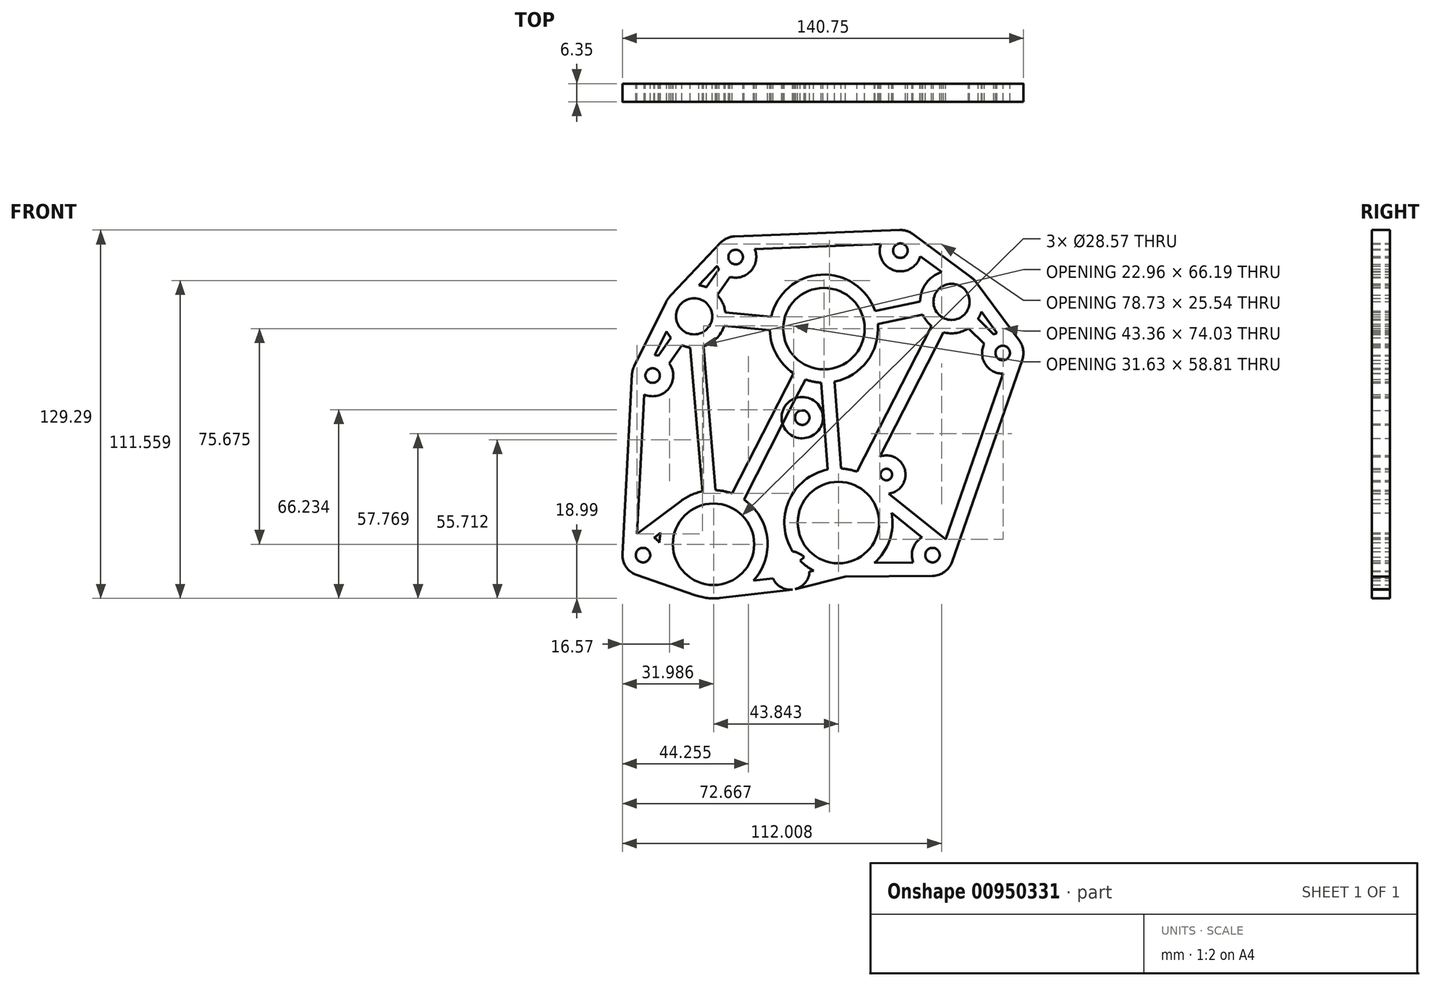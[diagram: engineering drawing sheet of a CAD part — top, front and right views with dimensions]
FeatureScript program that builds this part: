
annotation { "Feature Type Name" : "Feature", "Feature Type Description" : "" }
export const myFeature = defineFeature(function(context is Context, id is Id, definition is map)
    precondition{}
    {
        {
            var Q0;
            Q0=qCreatedBy(makeId("Front.planeOp"),FACE);
            var sketch = newSketch(context, id + "F0", { "sketchPlane" : qUnion([Q0])});
            skCircle(sketch, "E0", {"center": v(0, 0) * mm, "radius": 14.29 * mm});
            skCircle(sketch, "E1", {"center": v(-43.84, -7.62) * mm, "radius": 14.29 * mm});
            skCircle(sketch, "E2", {"center": v(-5.08, 68.06) * mm, "radius": 14.29 * mm});
            skCircle(sketch, "E3", {"center": v(39.71, 77.47) * mm, "radius": 6.35 * mm});
            skCircle(sketch, "E4", {"center": v(-50.65, 72.39) * mm, "radius": 6.35 * mm});
            skLineSegment(sketch, "E5.bottom", {"start": v(38.1, -19.05) * mm, "end": v(-76.2, -19.05) * mm, "construction": true});
            skLineSegment(sketch, "E5.top", {"start": v(38.1, 82.55) * mm, "end": v(-76.2, 82.55) * mm});
            skLineSegment(sketch, "E5.left", {"start": v(38.1, -19.05) * mm, "end": v(38.1, 82.55) * mm, "construction": true});
            skLineSegment(sketch, "E5.right", {"start": v(-76.2, -19.05) * mm, "end": v(-76.2, 82.55) * mm});
            skCircle(sketch, "E6", {"center": v(-43.84, -7.62) * mm, "radius": 18.99 * mm});
            skCircle(sketch, "E7", {"center": v(0, 0) * mm, "radius": 18.99 * mm});
            skLineSegment(sketch, "E8.bottom", {"start": v(-16.16, -9.97) * mm, "end": v(-25, -9.97) * mm});
            skLineSegment(sketch, "E8.top", {"start": v(-16.16, -5.27) * mm, "end": v(-25, -5.27) * mm});
            skLineSegment(sketch, "E8.left", {"start": v(-16.16, -9.97) * mm, "end": v(-16.16, -5.27) * mm});
            skLineSegment(sketch, "E8.right", {"start": v(-25, -9.97) * mm, "end": v(-25, -5.27) * mm});
            skCircle(sketch, "E9", {"center": v(-5.08, 68.06) * mm, "radius": 18.99 * mm});
            skCircle(sketch, "E10", {"center": v(-50.65, 72.39) * mm, "radius": 11.05 * mm});
            skLineSegment(sketch, "E11", {"start": v(-39.67, 73.7) * mm, "end": v(-40.12, 69.03) * mm, "construction": true});
            skLineSegment(sketch, "E12", {"start": v(-24.06, 67.5) * mm, "end": v(-23.61, 72.18) * mm, "construction": true});
            skLineSegment(sketch, "E13", {"start": v(-39.67, 73.7) * mm, "end": v(-23.61, 72.18) * mm});
            skLineSegment(sketch, "E14", {"start": v(-24.06, 67.5) * mm, "end": v(-40.12, 69.03) * mm});
            skLineSegment(sketch, "E15", {"start": v(-47.78, 10.95) * mm, "end": v(-43.1, 11.35) * mm, "construction": true});
            skLineSegment(sketch, "E16", {"start": v(-52.07, 61.43) * mm, "end": v(-47.39, 61.83) * mm, "construction": true});
            skLineSegment(sketch, "E17", {"start": v(-52.07, 61.43) * mm, "end": v(-47.78, 10.95) * mm});
            skLineSegment(sketch, "E18", {"start": v(-47.39, 61.83) * mm, "end": v(-43.1, 11.35) * mm});
            skCircle(sketch, "E19", {"center": v(39.71, 77.47) * mm, "radius": 11.05 * mm});
            skLineSegment(sketch, "E20.left", {"start": v(12.87, 74.23) * mm, "end": v(13.84, 69.63) * mm, "construction": true});
            skLineSegment(sketch, "E21", {"start": v(-15.76, 52.36) * mm, "end": v(-11.58, 50.22) * mm, "construction": true});
            skLineSegment(sketch, "E22", {"start": v(-37.35, 10.22) * mm, "end": v(-33.16, 8.08) * mm, "construction": true});
            skLineSegment(sketch, "E23", {"start": v(-37.35, 10.22) * mm, "end": v(-15.76, 52.36) * mm});
            skLineSegment(sketch, "E24", {"start": v(-11.58, 50.22) * mm, "end": v(-33.16, 8.08) * mm});
            skLineSegment(sketch, "E25", {"start": v(-5.08, 68.06) * mm, "end": v(0, 0) * mm, "construction": true});
            skLineSegment(sketch, "E26", {"start": v(-3.75, 18.61) * mm, "end": v(0.94, 18.96) * mm, "construction": true});
            skLineSegment(sketch, "E27", {"start": v(-6.02, 49.1) * mm, "end": v(-1.33, 49.44) * mm, "construction": true});
            skLineSegment(sketch, "E28", {"start": v(-6.02, 49.1) * mm, "end": v(-3.75, 18.61) * mm});
            skLineSegment(sketch, "E29", {"start": v(-1.33, 49.44) * mm, "end": v(0.94, 18.96) * mm});
            skLineSegment(sketch, "E30", {"start": v(6.5, 17.84) * mm, "end": v(10.69, 15.7) * mm, "construction": true});
            skLineSegment(sketch, "E31", {"start": v(32.7, 68.93) * mm, "end": v(36.88, 66.8) * mm, "construction": true});
            skLineSegment(sketch, "E32", {"start": v(32.7, 68.93) * mm, "end": v(6.5, 17.84) * mm});
            skLineSegment(sketch, "E33", {"start": v(36.88, 66.8) * mm, "end": v(10.69, 15.7) * mm});
            skCircle(sketch, "E34", {"center": v(-68.58, -11.43) * mm, "radius": 2.55 * mm});
            skCircle(sketch, "E35", {"center": v(33.02, -11.43) * mm, "radius": 2.55 * mm});
            skCircle(sketch, "E36", {"center": v(33.02, -11.43) * mm, "radius": 7.25 * mm});
            skCircle(sketch, "E37", {"center": v(-68.58, -11.43) * mm, "radius": 7.25 * mm});
            skLineSegment(sketch, "E38", {"start": v(-55.2, 7.6) * mm, "end": v(-72.92, -5.62) * mm});
            skLineSegment(sketch, "E39", {"start": v(-70.97, -18.28) * mm, "end": v(-50.09, -25.55) * mm});
            skLineSegment(sketch, "E40", {"start": v(11.88, 14.81) * mm, "end": v(37.56, -5.77) * mm});
            skCircle(sketch, "E41", {"center": v(-36.08, 93.2) * mm, "radius": 2.55 * mm});
            skCircle(sketch, "E42", {"center": v(-65.21, 51.58) * mm, "radius": 2.55 * mm});
            skLineSegment(sketch, "E43", {"start": v(-36.08, 93.2) * mm, "end": v(-65.21, 51.58) * mm, "construction": true});
            skCircle(sketch, "E44", {"center": v(57.67, 59.5) * mm, "radius": 2.55 * mm});
            skCircle(sketch, "E45", {"center": v(21.75, 95.43) * mm, "radius": 2.55 * mm});
            skCircle(sketch, "E46", {"center": v(57.67, 59.5) * mm, "radius": 7.25 * mm});
            skCircle(sketch, "E47", {"center": v(21.75, 95.43) * mm, "radius": 7.25 * mm});
            skCircle(sketch, "E48", {"center": v(-65.21, 51.58) * mm, "radius": 7.25 * mm});
            skCircle(sketch, "E49", {"center": v(-36.08, 93.2) * mm, "radius": 7.25 * mm});
            skLineSegment(sketch, "E50", {"start": v(-63.2, 58.55) * mm, "end": v(-59.35, 55.86) * mm, "construction": true});
            skLineSegment(sketch, "E51", {"start": v(-58.76, 64.9) * mm, "end": v(-54.91, 62.2) * mm, "construction": true});
            skLineSegment(sketch, "E52", {"start": v(-58.76, 64.9) * mm, "end": v(-63.2, 58.55) * mm});
            skLineSegment(sketch, "E53", {"start": v(-54.91, 62.2) * mm, "end": v(-59.35, 55.86) * mm});
            skLineSegment(sketch, "E54", {"start": v(49, 71.5) * mm, "end": v(45.68, 68.17) * mm, "construction": true});
            skLineSegment(sketch, "E55", {"start": v(51.16, 62.7) * mm, "end": v(54.48, 66.02) * mm, "construction": true});
            skLineSegment(sketch, "E56", {"start": v(51.16, 62.7) * mm, "end": v(45.68, 68.17) * mm});
            skLineSegment(sketch, "E57", {"start": v(54.48, 66.02) * mm, "end": v(49, 71.5) * mm});
            skLineSegment(sketch, "E58", {"start": v(-41.94, 88.92) * mm, "end": v(-38.09, 86.23) * mm, "construction": true});
            skLineSegment(sketch, "E59", {"start": v(-38.09, 86.23) * mm, "end": v(-42.53, 79.89) * mm});
            skLineSegment(sketch, "E60", {"start": v(-42.53, 79.89) * mm, "end": v(-46.38, 82.58) * mm, "construction": true});
            skLineSegment(sketch, "E61", {"start": v(-46.38, 82.58) * mm, "end": v(-41.94, 88.92) * mm});
            skCircle(sketch, "E62", {"center": v(0, 0) * mm, "radius": 23.81 * mm, "construction": true});
            skLineSegment(sketch, "E63", {"start": v(16.84, 16.84) * mm, "end": v(-16.84, -16.84) * mm});
            skCircle(sketch, "E64", {"center": v(-16.84, -16.84) * mm, "radius": 2.02 * mm});
            skCircle(sketch, "E65", {"center": v(16.84, 16.84) * mm, "radius": 2.02 * mm});
            skCircle(sketch, "E66", {"center": v(-16.84, -16.84) * mm, "radius": 6.72 * mm});
            skCircle(sketch, "E67", {"center": v(16.84, 16.84) * mm, "radius": 6.72 * mm});
            skLineSegment(sketch, "E68", {"start": v(21.75, 95.43) * mm, "end": v(57.67, 59.5) * mm, "construction": true});
            skLineSegment(sketch, "E69", {"start": v(12.87, 74.23) * mm, "end": v(28.66, 77.55) * mm});
            skLineSegment(sketch, "E70", {"start": v(13.84, 69.63) * mm, "end": v(29.63, 72.95) * mm});
            skLineSegment(sketch, "E71", {"start": v(29.63, 72.95) * mm, "end": v(28.66, 77.55) * mm, "construction": true});
            skLineSegment(sketch, "E72", {"start": v(18.7, 3.33) * mm, "end": v(29.32, -5.2) * mm});
            skLineSegment(sketch, "E73", {"start": v(26.26, -14.05) * mm, "end": v(12.64, -14.17) * mm});
            skLineSegment(sketch, "E74", {"start": v(-62.4, -3.64) * mm, "end": v(-64.67, -5.33) * mm});
            skLineSegment(sketch, "E75", {"start": v(-63, -16.07) * mm, "end": v(-60.35, -17) * mm});
            skCircle(sketch, "E76", {"center": v(-12.7, 36.83) * mm, "radius": 2.55 * mm});
            skCircle(sketch, "E77", {"center": v(-12.7, 36.83) * mm, "radius": 7.25 * mm});
            skLineSegment(sketch, "E78", {"start": v(-75.82, -11.04) * mm, "end": v(-72.46, 51.97) * mm});
            skLineSegment(sketch, "E79", {"start": v(-71.7, 54.8) * mm, "end": v(-60.54, 77.3) * mm});
            skLineSegment(sketch, "E80", {"start": v(-58.65, 80) * mm, "end": v(-41.33, 98.2) * mm});
            skLineSegment(sketch, "E81", {"start": v(-49, 83.32) * mm, "end": v(-42.6, 90.04) * mm});
            skLineSegment(sketch, "E82", {"start": v(-60.35, 67.11) * mm, "end": v(-64.48, 58.8) * mm});
            skLineSegment(sketch, "E83", {"start": v(-36.36, 100.44) * mm, "end": v(21.47, 102.68) * mm});
            skLineSegment(sketch, "E84", {"start": v(-29.4, 96) * mm, "end": v(14.87, 97.72) * mm});
            skLineSegment(sketch, "E85", {"start": v(26.06, 101.27) * mm, "end": v(46.27, 86.36) * mm});
            skLineSegment(sketch, "E86", {"start": v(28.73, 93.46) * mm, "end": v(36.2, 87.95) * mm});
            skLineSegment(sketch, "E87", {"start": v(48.6, 84.03) * mm, "end": v(63.5, 63.81) * mm});
            skLineSegment(sketch, "E88", {"start": v(50.19, 73.96) * mm, "end": v(55.7, 66.49) * mm});
            skLineSegment(sketch, "E89", {"start": v(39.87, -13.81) * mm, "end": v(64.52, 57.13) * mm});
            skLineSegment(sketch, "E90", {"start": v(57.86, 52.26) * mm, "end": v(37.66, -5.86) * mm});
            skLineSegment(sketch, "E91", {"start": v(-68.13, 44.94) * mm, "end": v(-70.77, -4.52) * mm});
            skLineSegment(sketch, "E92", {"start": v(33.09, -18.68) * mm, "end": v(0.18, -18.99) * mm});
            skLineSegment(sketch, "E93", {"start": v(-15.21, -23.36) * mm, "end": v(4.59, -18.42) * mm});
            skLineSegment(sketch, "E94", {"start": v(-16.06, -23.51) * mm, "end": v(-41.66, -26.48) * mm});
            skLineSegment(sketch, "E95", {"start": v(-29.78, -20.37) * mm, "end": v(-22.97, -19.58) * mm});
            skLineSegment(sketch, "E96", {"start": v(-10.13, -17.25) * mm, "end": v(-8.68, -16.89) * mm});
            skSolve(sketch);
        }
        {
            var Q0;
            {var subQ0=sQuery(id+"F0.wireOp",EDGE,"E53");Q0=makeQuery(id+"F0.imprint","IMPRINT",FACE,{"disambiguationData":[TD([[makeQuery(id+"F0.imprint","IMPRINT",EDGE,{"derivedFrom":subQ0}),-1.0]])]});}
            var Q1;
            {var subQ0=sQuery(id+"F0.wireOp",EDGE,"E59");Q1=makeQuery(id+"F0.imprint","IMPRINT",FACE,{"disambiguationData":[TD([[makeQuery(id+"F0.imprint","IMPRINT",EDGE,{"derivedFrom":subQ0}),-1.0]])]});}
            var Q2;
            {var subQ0=sQuery(id+"F0.wireOp",EDGE,"E61");Q2=makeQuery(id+"F0.imprint","IMPRINT",FACE,{"disambiguationData":[TD([[makeQuery(id+"F0.imprint","IMPRINT",EDGE,{"derivedFrom":subQ0}),-1.0]])]});}
            var Q3;
            {var subQ1=sQuery(id+"F0.wireOp",EDGE,"E9");var subQ3=sQuery(id+"F0.wireOp",EDGE,"E25");var subQ4=makeQuery(id+"F0.imprint","INTERSECT",VERTEX,{"derivedFrom":[subQ1,subQ3]});Q3=makeQuery(id+"F0.imprint","IMPRINT",FACE,{"disambiguationData":[TD([[makeQuery(id+"F0.imprint","IMPRINT",EDGE,{"disambiguationData":[TD([[subQ4,-1.0]])],"derivedFrom":subQ3}),1.0]])]});}
            var Q4;
            {var subQ1=sQuery(id+"F0.wireOp",EDGE,"E9");var subQ3=sQuery(id+"F0.wireOp",EDGE,"E25");var subQ4=makeQuery(id+"F0.imprint","INTERSECT",VERTEX,{"derivedFrom":[subQ1,subQ3]});Q4=makeQuery(id+"F0.imprint","IMPRINT",FACE,{"disambiguationData":[TD([[makeQuery(id+"F0.imprint","IMPRINT",EDGE,{"disambiguationData":[TD([[subQ4,-1.0]])],"derivedFrom":subQ3}),-1.0]])]});}
            var Q5;
            {var subQ0=sQuery(id+"F0.wireOp",EDGE,"E20.right");Q5=makeQuery(id+"F0.imprint","IMPRINT",FACE,{"disambiguationData":[TD([[makeQuery(id+"F0.imprint","IMPRINT",EDGE,{"derivedFrom":subQ0}),1.0]])]});}
            var Q6;
            {var subQ0=sQuery(id+"F0.wireOp",EDGE,"E47");var subQ1=sQuery(id+"F0.wireOp",EDGE,"E5.top");var subQ2=makeQuery(id+"F0.imprint","INTERSECT",VERTEX,{"disambiguationData":[OD(0.0)],"derivedFrom":[subQ1,subQ0]});Q6=makeQuery(id+"F0.imprint","IMPRINT",FACE,{"disambiguationData":[TD([[makeQuery(id+"F0.imprint","IMPRINT",EDGE,{"disambiguationData":[TD([[subQ2,-1.0]])],"derivedFrom":subQ1}),-1.0]])]});}
            var Q7;
            {var subQ0=sQuery(id+"F0.wireOp",EDGE,"E48");var subQ1=sQuery(id+"F0.wireOp",EDGE,"E5.right");var subQ2=makeQuery(id+"F0.imprint","INTERSECT",VERTEX,{"disambiguationData":[OD(0.0)],"derivedFrom":[subQ1,subQ0]});Q7=makeQuery(id+"F0.imprint","IMPRINT",FACE,{"disambiguationData":[TD([[makeQuery(id+"F0.imprint","IMPRINT",EDGE,{"disambiguationData":[TD([[subQ2,-1.0]])],"derivedFrom":subQ1}),1.0]])]});}
            var Q8;
            {var subQ1=sQuery(id+"F0.wireOp",EDGE,"E5.bottom");var subQ8=sQuery(id+"F0.wireOp",EDGE,"E66");var subQ11=makeQuery(id+"F0.imprint","INTERSECT",VERTEX,{"disambiguationData":[OD(1.0)],"derivedFrom":[subQ1,subQ8]});Q8=makeQuery(id+"F0.imprint","IMPRINT",FACE,{"disambiguationData":[TD([[makeQuery(id+"F0.imprint","IMPRINT",EDGE,{"disambiguationData":[TD([[subQ11,-1.0]])],"derivedFrom":subQ1}),-1.0]])]});}
            var Q9;
            {var subQ0=sQuery(id+"F0.wireOp",EDGE,"E66");var subQ1=sQuery(id+"F0.wireOp",EDGE,"E5.bottom");var subQ2=makeQuery(id+"F0.imprint","INTERSECT",VERTEX,{"disambiguationData":[OD(0.0)],"derivedFrom":[subQ1,subQ0]});Q9=makeQuery(id+"F0.imprint","IMPRINT",FACE,{"disambiguationData":[TD([[makeQuery(id+"F0.imprint","IMPRINT",EDGE,{"disambiguationData":[TD([[subQ2,1.0]])],"derivedFrom":subQ1}),1.0]])]});}
            var Q10;
            Q10=makeQuery(id+"F0.imprint","IMPRINT",FACE,{"disambiguationData":[TD([[makeQuery(id+"F0.imprint","IMPRINT",EDGE,{"derivedFrom":sQuery(id+"F0.wireOp",EDGE,"E44")}),-1.0]])]});
            var Q11;
            {var subQ0=sQuery(id+"F0.wireOp",EDGE,"E67");var subQ1=sQuery(id+"F0.wireOp",EDGE,"E46");var subQ2=makeQuery(id+"F0.imprint","INTERSECT",VERTEX,{"disambiguationData":[OD(0.0)],"derivedFrom":[subQ1,subQ0]});Q11=makeQuery(id+"F0.imprint","IMPRINT",FACE,{"disambiguationData":[TD([[makeQuery(id+"F0.imprint","IMPRINT",EDGE,{"disambiguationData":[TD([[subQ2,-1.0]])],"derivedFrom":subQ1}),1.0]])]});}
            var Q12;
            {var subQ0=sQuery(id+"F0.wireOp",EDGE,"E56");Q12=makeQuery(id+"F0.imprint","IMPRINT",FACE,{"disambiguationData":[TD([[makeQuery(id+"F0.imprint","IMPRINT",EDGE,{"derivedFrom":subQ0}),-1.0]])]});}
            var Q13;
            {var subQ3=sQuery(id+"F0.wireOp",EDGE,"VYO2AEf5-A0on-8gMK-xq1d-WM22INMwvEMz");var subQ5=sQuery(id+"F0.wireOp",EDGE,"E3");var subQ6=makeQuery(id+"F0.imprint","INTERSECT",VERTEX,{"derivedFrom":[subQ5,subQ3]});Q13=makeQuery(id+"F0.imprint","IMPRINT",FACE,{"disambiguationData":[TD([[makeQuery(id+"F0.imprint","IMPRINT",EDGE,{"disambiguationData":[TD([[subQ6,-1.0]])],"derivedFrom":subQ5}),-1.0]])]});}
            var Q14;
            {var subQ1=sQuery(id+"F0.wireOp",EDGE,"E19");var subQ3=sQuery(id+"F0.wireOp",EDGE,"VYO2AEf5-A0on-8gMK-xq1d-WM22INMwvEMz");var subQ4=makeQuery(id+"F0.imprint","INTERSECT",VERTEX,{"derivedFrom":[subQ1,subQ3]});Q14=makeQuery(id+"F0.imprint","IMPRINT",FACE,{"disambiguationData":[TD([[makeQuery(id+"F0.imprint","IMPRINT",EDGE,{"disambiguationData":[TD([[subQ4,-1.0]])],"derivedFrom":subQ3}),-1.0]])]});}
            var Q15;
            {var subQ1=sQuery(id+"F0.wireOp",EDGE,"E7");var subQ3=sQuery(id+"F0.wireOp",EDGE,"VYO2AEf5-A0on-8gMK-xq1d-WM22INMwvEMz");var subQ4=makeQuery(id+"F0.imprint","INTERSECT",VERTEX,{"derivedFrom":[subQ1,subQ3]});Q15=makeQuery(id+"F0.imprint","IMPRINT",FACE,{"disambiguationData":[TD([[makeQuery(id+"F0.imprint","IMPRINT",EDGE,{"disambiguationData":[TD([[subQ4,1.0]])],"derivedFrom":subQ3}),1.0]])]});}
            var Q16;
            {var subQ1=sQuery(id+"F0.wireOp",EDGE,"E7");var subQ3=sQuery(id+"F0.wireOp",EDGE,"VYO2AEf5-A0on-8gMK-xq1d-WM22INMwvEMz");var subQ4=makeQuery(id+"F0.imprint","INTERSECT",VERTEX,{"derivedFrom":[subQ1,subQ3]});Q16=makeQuery(id+"F0.imprint","IMPRINT",FACE,{"disambiguationData":[TD([[makeQuery(id+"F0.imprint","IMPRINT",EDGE,{"disambiguationData":[TD([[subQ4,1.0]])],"derivedFrom":subQ3}),-1.0]])]});}
            var Q17;
            {var subQ0=sQuery(id+"F0.wireOp",EDGE,"E7");var subQ1=makeQuery(id+"F0.imprint","INTERSECT",VERTEX,{"derivedFrom":[subQ0,sQuery(id+"F0.wireOp",EDGE,"E40")]});Q17=makeQuery(id+"F0.imprint","IMPRINT",FACE,{"disambiguationData":[TD([[makeQuery(id+"F0.imprint","IMPRINT",EDGE,{"disambiguationData":[TD([[subQ1,1.0]])],"derivedFrom":subQ0}),1.0]])]});}
            var Q18;
            {var subQ3=sQuery(id+"F0.wireOp",EDGE,"E63");var subQ5=sQuery(id+"F0.wireOp",EDGE,"E40");var subQ6=makeQuery(id+"F0.imprint","INTERSECT",VERTEX,{"derivedFrom":[subQ5,subQ3]});Q18=makeQuery(id+"F0.imprint","IMPRINT",FACE,{"disambiguationData":[TD([[makeQuery(id+"F0.imprint","IMPRINT",EDGE,{"disambiguationData":[TD([[subQ6,-1.0]])],"derivedFrom":subQ5}),1.0]])]});}
            var Q19;
            {var subQ5=sQuery(id+"F0.wireOp",EDGE,"E7");var subQ8=sQuery(id+"F0.wireOp",EDGE,"E40");var subQ11=makeQuery(id+"F0.imprint","INTERSECT",VERTEX,{"derivedFrom":[subQ5,subQ8]});Q19=makeQuery(id+"F0.imprint","IMPRINT",FACE,{"disambiguationData":[TD([[makeQuery(id+"F0.imprint","IMPRINT",EDGE,{"disambiguationData":[TD([[subQ11,-1.0]])],"derivedFrom":subQ5}),-1.0]])]});}
            var Q20;
            {var subQ1=sQuery(id+"F0.wireOp",EDGE,"E7");var subQ3=sQuery(id+"F0.wireOp",EDGE,"E25");var subQ4=makeQuery(id+"F0.imprint","INTERSECT",VERTEX,{"derivedFrom":[subQ1,subQ3]});Q20=makeQuery(id+"F0.imprint","IMPRINT",FACE,{"disambiguationData":[TD([[makeQuery(id+"F0.imprint","IMPRINT",EDGE,{"disambiguationData":[TD([[subQ4,1.0]])],"derivedFrom":subQ3}),-1.0]])]});}
            var Q21;
            {var subQ1=sQuery(id+"F0.wireOp",EDGE,"E7");var subQ3=sQuery(id+"F0.wireOp",EDGE,"E25");var subQ4=makeQuery(id+"F0.imprint","INTERSECT",VERTEX,{"derivedFrom":[subQ1,subQ3]});Q21=makeQuery(id+"F0.imprint","IMPRINT",FACE,{"disambiguationData":[TD([[makeQuery(id+"F0.imprint","IMPRINT",EDGE,{"disambiguationData":[TD([[subQ4,1.0]])],"derivedFrom":subQ3}),1.0]])]});}
            var Q22;
            {var subQ1=sQuery(id+"F0.wireOp",EDGE,"E19");var subQ3=sQuery(id+"F0.wireOp",EDGE,"VYO2AEf5-A0on-8gMK-xq1d-WM22INMwvEMz");var subQ4=makeQuery(id+"F0.imprint","INTERSECT",VERTEX,{"derivedFrom":[subQ1,subQ3]});Q22=makeQuery(id+"F0.imprint","IMPRINT",FACE,{"disambiguationData":[TD([[makeQuery(id+"F0.imprint","IMPRINT",EDGE,{"disambiguationData":[TD([[subQ4,-1.0]])],"derivedFrom":subQ3}),1.0]])]});}
            var Q23;
            {var subQ0=sQuery(id+"F0.wireOp",EDGE,"E63");var subQ1=sQuery(id+"F0.wireOp",EDGE,"E7");var subQ2=makeQuery(id+"F0.imprint","INTERSECT",VERTEX,{"disambiguationData":[OD(0.0)],"derivedFrom":[subQ1,subQ0]});Q23=makeQuery(id+"F0.imprint","IMPRINT",FACE,{"disambiguationData":[TD([[makeQuery(id+"F0.imprint","IMPRINT",EDGE,{"disambiguationData":[TD([[subQ2,1.0]])],"derivedFrom":subQ1}),-1.0]])]});}
            var Q24;
            {var subQ3=sQuery(id+"F0.wireOp",EDGE,"VYO2AEf5-A0on-8gMK-xq1d-WM22INMwvEMz");var subQ5=sQuery(id+"F0.wireOp",EDGE,"E0");var subQ6=makeQuery(id+"F0.imprint","INTERSECT",VERTEX,{"derivedFrom":[subQ5,subQ3]});Q24=makeQuery(id+"F0.imprint","IMPRINT",FACE,{"disambiguationData":[TD([[makeQuery(id+"F0.imprint","IMPRINT",EDGE,{"disambiguationData":[TD([[subQ6,1.0]])],"derivedFrom":subQ5}),-1.0]])]});}
            var Q25;
            {var subQ5=sQuery(id+"F0.wireOp",EDGE,"E0");var subQ9=sQuery(id+"F0.wireOp",EDGE,"VYO2AEf5-A0on-8gMK-xq1d-WM22INMwvEMz");var subQ10=makeQuery(id+"F0.imprint","INTERSECT",VERTEX,{"derivedFrom":[subQ5,subQ9]});Q25=makeQuery(id+"F0.imprint","IMPRINT",FACE,{"disambiguationData":[TD([[makeQuery(id+"F0.imprint","IMPRINT",EDGE,{"disambiguationData":[TD([[subQ10,-1.0]])],"derivedFrom":subQ5}),-1.0]])]});}
            var Q26;
            {var subQ1=sQuery(id+"F0.wireOp",EDGE,"E7");var subQ3=sQuery(id+"F0.wireOp",EDGE,"VYO2AEf5-A0on-8gMK-xq1d-WM22INMwvEMz");var subQ4=makeQuery(id+"F0.imprint","INTERSECT",VERTEX,{"derivedFrom":[subQ1,subQ3]});Q26=makeQuery(id+"F0.imprint","IMPRINT",FACE,{"disambiguationData":[TD([[makeQuery(id+"F0.imprint","IMPRINT",EDGE,{"disambiguationData":[TD([[subQ4,-1.0]])],"derivedFrom":subQ3}),-1.0]])]});}
            var Q27;
            {var subQ1=sQuery(id+"F0.wireOp",EDGE,"E7");var subQ3=sQuery(id+"F0.wireOp",EDGE,"VYO2AEf5-A0on-8gMK-xq1d-WM22INMwvEMz");var subQ4=makeQuery(id+"F0.imprint","INTERSECT",VERTEX,{"derivedFrom":[subQ1,subQ3]});Q27=makeQuery(id+"F0.imprint","IMPRINT",FACE,{"disambiguationData":[TD([[makeQuery(id+"F0.imprint","IMPRINT",EDGE,{"disambiguationData":[TD([[subQ4,-1.0]])],"derivedFrom":subQ3}),1.0]])]});}
            var Q28;
            {var subQ1=sQuery(id+"F0.wireOp",EDGE,"E7");var subQ3=sQuery(id+"F0.wireOp",EDGE,"E25");var subQ4=makeQuery(id+"F0.imprint","INTERSECT",VERTEX,{"derivedFrom":[subQ1,subQ3]});Q28=makeQuery(id+"F0.imprint","IMPRINT",FACE,{"disambiguationData":[TD([[makeQuery(id+"F0.imprint","IMPRINT",EDGE,{"disambiguationData":[TD([[subQ4,-1.0]])],"derivedFrom":subQ3}),1.0]])]});}
            var Q29;
            {var subQ1=sQuery(id+"F0.wireOp",EDGE,"E7");var subQ3=sQuery(id+"F0.wireOp",EDGE,"E25");var subQ4=makeQuery(id+"F0.imprint","INTERSECT",VERTEX,{"derivedFrom":[subQ1,subQ3]});Q29=makeQuery(id+"F0.imprint","IMPRINT",FACE,{"disambiguationData":[TD([[makeQuery(id+"F0.imprint","IMPRINT",EDGE,{"disambiguationData":[TD([[subQ4,-1.0]])],"derivedFrom":subQ3}),-1.0]])]});}
            var Q30;
            {var subQ0=sQuery(id+"F0.wireOp",EDGE,"E55");var subQ1=sQuery(id+"F0.wireOp",EDGE,"QEKIW3ol-zFeQ-8mqy-IqnZ-AELnMHeZj292");var subQ2=makeQuery(id+"F0.imprint","INTERSECT",VERTEX,{"derivedFrom":[subQ1,subQ0]});Q30=makeQuery(id+"F0.imprint","IMPRINT",FACE,{"disambiguationData":[TD([[makeQuery(id+"F0.imprint","IMPRINT",EDGE,{"disambiguationData":[TD([[subQ2,1.0]])],"derivedFrom":subQ1}),-1.0]])]});}
            var Q31;
            {var subQ0=sQuery(id+"F0.wireOp",EDGE,"E55");var subQ1=sQuery(id+"F0.wireOp",EDGE,"QEKIW3ol-zFeQ-8mqy-IqnZ-AELnMHeZj292");var subQ2=makeQuery(id+"F0.imprint","INTERSECT",VERTEX,{"derivedFrom":[subQ1,subQ0]});Q31=makeQuery(id+"F0.imprint","IMPRINT",FACE,{"disambiguationData":[TD([[makeQuery(id+"F0.imprint","IMPRINT",EDGE,{"disambiguationData":[TD([[subQ2,1.0]])],"derivedFrom":subQ1}),1.0]])]});}
            var Q32;
            {var subQ1=sQuery(id+"F0.wireOp",EDGE,"E19");var subQ3=sQuery(id+"F0.wireOp",EDGE,"VYO2AEf5-A0on-8gMK-xq1d-WM22INMwvEMz");var subQ4=makeQuery(id+"F0.imprint","INTERSECT",VERTEX,{"derivedFrom":[subQ1,subQ3]});Q32=makeQuery(id+"F0.imprint","IMPRINT",FACE,{"disambiguationData":[TD([[makeQuery(id+"F0.imprint","IMPRINT",EDGE,{"disambiguationData":[TD([[subQ4,1.0]])],"derivedFrom":subQ3}),-1.0]])]});}
            var Q33;
            {var subQ1=sQuery(id+"F0.wireOp",EDGE,"E19");var subQ3=sQuery(id+"F0.wireOp",EDGE,"VYO2AEf5-A0on-8gMK-xq1d-WM22INMwvEMz");var subQ4=makeQuery(id+"F0.imprint","INTERSECT",VERTEX,{"derivedFrom":[subQ1,subQ3]});Q33=makeQuery(id+"F0.imprint","IMPRINT",FACE,{"disambiguationData":[TD([[makeQuery(id+"F0.imprint","IMPRINT",EDGE,{"disambiguationData":[TD([[subQ4,1.0]])],"derivedFrom":subQ3}),1.0]])]});}
            var Q34;
            {var subQ1=sQuery(id+"F0.wireOp",EDGE,"E19");var subQ3=sQuery(id+"F0.wireOp",EDGE,"QEKIW3ol-zFeQ-8mqy-IqnZ-AELnMHeZj292");var subQ4=makeQuery(id+"F0.imprint","INTERSECT",VERTEX,{"disambiguationData":[OD(1.0)],"derivedFrom":[subQ1,subQ3]});Q34=makeQuery(id+"F0.imprint","IMPRINT",FACE,{"disambiguationData":[TD([[makeQuery(id+"F0.imprint","IMPRINT",EDGE,{"disambiguationData":[TD([[subQ4,1.0]])],"derivedFrom":subQ3}),-1.0]])]});}
            var Q35;
            {var subQ1=sQuery(id+"F0.wireOp",EDGE,"E19");var subQ3=sQuery(id+"F0.wireOp",EDGE,"QEKIW3ol-zFeQ-8mqy-IqnZ-AELnMHeZj292");var subQ4=makeQuery(id+"F0.imprint","INTERSECT",VERTEX,{"disambiguationData":[OD(1.0)],"derivedFrom":[subQ1,subQ3]});Q35=makeQuery(id+"F0.imprint","IMPRINT",FACE,{"disambiguationData":[TD([[makeQuery(id+"F0.imprint","IMPRINT",EDGE,{"disambiguationData":[TD([[subQ4,1.0]])],"derivedFrom":subQ3}),1.0]])]});}
            var Q36;
            {var subQ0=sQuery(id+"F0.wireOp",EDGE,"E20.left");Q36=makeQuery(id+"F0.imprint","IMPRINT",FACE,{"disambiguationData":[TD([[makeQuery(id+"F0.imprint","IMPRINT",EDGE,{"derivedFrom":subQ0}),1.0]])]});}
            var Q37;
            {var subQ0=sQuery(id+"F0.wireOp",EDGE,"E20.right");Q37=makeQuery(id+"F0.imprint","IMPRINT",FACE,{"disambiguationData":[TD([[makeQuery(id+"F0.imprint","IMPRINT",EDGE,{"derivedFrom":subQ0}),-1.0]])]});}
            var Q38;
            {var subQ1=sQuery(id+"F0.wireOp",EDGE,"E19");var subQ3=sQuery(id+"F0.wireOp",EDGE,"QEKIW3ol-zFeQ-8mqy-IqnZ-AELnMHeZj292");var subQ4=makeQuery(id+"F0.imprint","INTERSECT",VERTEX,{"disambiguationData":[OD(0.0)],"derivedFrom":[subQ1,subQ3]});Q38=makeQuery(id+"F0.imprint","IMPRINT",FACE,{"disambiguationData":[TD([[makeQuery(id+"F0.imprint","IMPRINT",EDGE,{"disambiguationData":[TD([[subQ4,-1.0]])],"derivedFrom":subQ3}),-1.0]])]});}
            var Q39;
            {var subQ1=sQuery(id+"F0.wireOp",EDGE,"E19");var subQ3=sQuery(id+"F0.wireOp",EDGE,"QEKIW3ol-zFeQ-8mqy-IqnZ-AELnMHeZj292");var subQ4=makeQuery(id+"F0.imprint","INTERSECT",VERTEX,{"disambiguationData":[OD(0.0)],"derivedFrom":[subQ1,subQ3]});Q39=makeQuery(id+"F0.imprint","IMPRINT",FACE,{"disambiguationData":[TD([[makeQuery(id+"F0.imprint","IMPRINT",EDGE,{"disambiguationData":[TD([[subQ4,-1.0]])],"derivedFrom":subQ3}),1.0]])]});}
            var Q40;
            {var subQ0=sQuery(id+"F0.wireOp",EDGE,"PWp1EvH2-qaDC-40DG-vf9U-hu9o8N1M8XT3");var subQ1=sQuery(id+"F0.wireOp",EDGE,"QEKIW3ol-zFeQ-8mqy-IqnZ-AELnMHeZj292");var subQ2=makeQuery(id+"F0.imprint","INTERSECT",VERTEX,{"derivedFrom":[subQ1,subQ0]});Q40=makeQuery(id+"F0.imprint","IMPRINT",FACE,{"disambiguationData":[TD([[makeQuery(id+"F0.imprint","IMPRINT",EDGE,{"disambiguationData":[TD([[subQ2,-1.0]])],"derivedFrom":subQ1}),1.0]])]});}
            var Q41;
            {var subQ0=sQuery(id+"F0.wireOp",EDGE,"PWp1EvH2-qaDC-40DG-vf9U-hu9o8N1M8XT3");var subQ1=sQuery(id+"F0.wireOp",EDGE,"QEKIW3ol-zFeQ-8mqy-IqnZ-AELnMHeZj292");var subQ2=makeQuery(id+"F0.imprint","INTERSECT",VERTEX,{"derivedFrom":[subQ1,subQ0]});Q41=makeQuery(id+"F0.imprint","IMPRINT",FACE,{"disambiguationData":[TD([[makeQuery(id+"F0.imprint","IMPRINT",EDGE,{"disambiguationData":[TD([[subQ2,-1.0]])],"derivedFrom":subQ1}),-1.0]])]});}
            var Q42;
            {var subQ3=sQuery(id+"F0.wireOp",EDGE,"E13");Q42=makeQuery(id+"F0.imprint","IMPRINT",FACE,{"disambiguationData":[TD([[makeQuery(id+"F0.imprint","IMPRINT",EDGE,{"derivedFrom":subQ3}),-1.0]])]});}
            var Q43;
            {var subQ0=sQuery(id+"F0.wireOp",EDGE,"E50");var subQ1=sQuery(id+"F0.wireOp",EDGE,"E43");var subQ2=makeQuery(id+"F0.imprint","INTERSECT",VERTEX,{"derivedFrom":[subQ1,subQ0]});Q43=makeQuery(id+"F0.imprint","IMPRINT",FACE,{"disambiguationData":[TD([[makeQuery(id+"F0.imprint","IMPRINT",EDGE,{"disambiguationData":[TD([[subQ2,1.0]])],"derivedFrom":subQ1}),-1.0]])]});}
            var Q44;
            {var subQ0=sQuery(id+"F0.wireOp",EDGE,"E50");var subQ1=sQuery(id+"F0.wireOp",EDGE,"E43");var subQ2=makeQuery(id+"F0.imprint","INTERSECT",VERTEX,{"derivedFrom":[subQ1,subQ0]});Q44=makeQuery(id+"F0.imprint","IMPRINT",FACE,{"disambiguationData":[TD([[makeQuery(id+"F0.imprint","IMPRINT",EDGE,{"disambiguationData":[TD([[subQ2,1.0]])],"derivedFrom":subQ1}),1.0]])]});}
            var Q45;
            {var subQ1=sQuery(id+"F0.wireOp",EDGE,"E10");var subQ3=sQuery(id+"F0.wireOp",EDGE,"E43");var subQ4=makeQuery(id+"F0.imprint","INTERSECT",VERTEX,{"disambiguationData":[OD(1.0)],"derivedFrom":[subQ1,subQ3]});Q45=makeQuery(id+"F0.imprint","IMPRINT",FACE,{"disambiguationData":[TD([[makeQuery(id+"F0.imprint","IMPRINT",EDGE,{"disambiguationData":[TD([[subQ4,1.0]])],"derivedFrom":subQ3}),-1.0]])]});}
            var Q46;
            {var subQ1=sQuery(id+"F0.wireOp",EDGE,"E10");var subQ3=sQuery(id+"F0.wireOp",EDGE,"E43");var subQ4=makeQuery(id+"F0.imprint","INTERSECT",VERTEX,{"disambiguationData":[OD(1.0)],"derivedFrom":[subQ1,subQ3]});Q46=makeQuery(id+"F0.imprint","IMPRINT",FACE,{"disambiguationData":[TD([[makeQuery(id+"F0.imprint","IMPRINT",EDGE,{"disambiguationData":[TD([[subQ4,1.0]])],"derivedFrom":subQ3}),1.0]])]});}
            var Q47;
            {var subQ1=sQuery(id+"F0.wireOp",EDGE,"E10");var subQ3=sQuery(id+"F0.wireOp",EDGE,"DAOfpOoV-ewgr-EIjx-MOBx-atSazLD0E7Ij");var subQ4=makeQuery(id+"F0.imprint","INTERSECT",VERTEX,{"derivedFrom":[subQ1,subQ3]});Q47=makeQuery(id+"F0.imprint","IMPRINT",FACE,{"disambiguationData":[TD([[makeQuery(id+"F0.imprint","IMPRINT",EDGE,{"disambiguationData":[TD([[subQ4,1.0]])],"derivedFrom":subQ3}),-1.0]])]});}
            var Q48;
            {var subQ1=sQuery(id+"F0.wireOp",EDGE,"E10");var subQ3=sQuery(id+"F0.wireOp",EDGE,"DAOfpOoV-ewgr-EIjx-MOBx-atSazLD0E7Ij");var subQ4=makeQuery(id+"F0.imprint","INTERSECT",VERTEX,{"derivedFrom":[subQ1,subQ3]});Q48=makeQuery(id+"F0.imprint","IMPRINT",FACE,{"disambiguationData":[TD([[makeQuery(id+"F0.imprint","IMPRINT",EDGE,{"disambiguationData":[TD([[subQ4,1.0]])],"derivedFrom":subQ3}),1.0]])]});}
            var Q49;
            {var subQ0=sQuery(id+"F0.wireOp",EDGE,"E11");Q49=makeQuery(id+"F0.imprint","IMPRINT",FACE,{"disambiguationData":[TD([[makeQuery(id+"F0.imprint","IMPRINT",EDGE,{"derivedFrom":subQ0}),1.0]])]});}
            var Q50;
            {var subQ0=sQuery(id+"F0.wireOp",EDGE,"E12");Q50=makeQuery(id+"F0.imprint","IMPRINT",FACE,{"disambiguationData":[TD([[makeQuery(id+"F0.imprint","IMPRINT",EDGE,{"derivedFrom":subQ0}),1.0]])]});}
            var Q51;
            {var subQ0=sQuery(id+"F0.wireOp",EDGE,"E63");var subQ1=sQuery(id+"F0.wireOp",EDGE,"E7");var subQ2=makeQuery(id+"F0.imprint","INTERSECT",VERTEX,{"disambiguationData":[OD(1.0)],"derivedFrom":[subQ1,subQ0]});Q51=makeQuery(id+"F0.imprint","IMPRINT",FACE,{"disambiguationData":[TD([[makeQuery(id+"F0.imprint","IMPRINT",EDGE,{"disambiguationData":[TD([[subQ2,-1.0]])],"derivedFrom":subQ1}),1.0]])]});}
            var Q52;
            {var subQ0=sQuery(id+"F0.wireOp",EDGE,"E66");var subQ1=sQuery(id+"F0.wireOp",EDGE,"E5.bottom");var subQ2=makeQuery(id+"F0.imprint","INTERSECT",VERTEX,{"disambiguationData":[OD(1.0)],"derivedFrom":[subQ1,subQ0]});Q52=makeQuery(id+"F0.imprint","IMPRINT",FACE,{"disambiguationData":[TD([[makeQuery(id+"F0.imprint","IMPRINT",EDGE,{"disambiguationData":[TD([[subQ2,-1.0]])],"derivedFrom":subQ1}),1.0]])]});}
            var Q53;
            {var subQ1=sQuery(id+"F0.wireOp",EDGE,"E6");var subQ3=sQuery(id+"F0.wireOp",EDGE,"DAOfpOoV-ewgr-EIjx-MOBx-atSazLD0E7Ij");var subQ4=makeQuery(id+"F0.imprint","INTERSECT",VERTEX,{"derivedFrom":[subQ1,subQ3]});Q53=makeQuery(id+"F0.imprint","IMPRINT",FACE,{"disambiguationData":[TD([[makeQuery(id+"F0.imprint","IMPRINT",EDGE,{"disambiguationData":[TD([[subQ4,-1.0]])],"derivedFrom":subQ3}),-1.0]])]});}
            var Q54;
            {var subQ1=sQuery(id+"F0.wireOp",EDGE,"E6");var subQ3=sQuery(id+"F0.wireOp",EDGE,"DAOfpOoV-ewgr-EIjx-MOBx-atSazLD0E7Ij");var subQ4=makeQuery(id+"F0.imprint","INTERSECT",VERTEX,{"derivedFrom":[subQ1,subQ3]});Q54=makeQuery(id+"F0.imprint","IMPRINT",FACE,{"disambiguationData":[TD([[makeQuery(id+"F0.imprint","IMPRINT",EDGE,{"disambiguationData":[TD([[subQ4,-1.0]])],"derivedFrom":subQ3}),1.0]])]});}
            var Q55;
            {var subQ1=sQuery(id+"F0.wireOp",EDGE,"E6");var subQ3=sQuery(id+"F0.wireOp",EDGE,"iRxx2WUk-GL6D-XYzB-BCGU-y0DAeOXOSD90");var subQ4=makeQuery(id+"F0.imprint","INTERSECT",VERTEX,{"derivedFrom":[subQ1,subQ3]});Q55=makeQuery(id+"F0.imprint","IMPRINT",FACE,{"disambiguationData":[TD([[makeQuery(id+"F0.imprint","IMPRINT",EDGE,{"disambiguationData":[TD([[subQ4,1.0]])],"derivedFrom":subQ3}),1.0]])]});}
            var Q56;
            {var subQ1=sQuery(id+"F0.wireOp",EDGE,"E6");var subQ3=sQuery(id+"F0.wireOp",EDGE,"iRxx2WUk-GL6D-XYzB-BCGU-y0DAeOXOSD90");var subQ4=makeQuery(id+"F0.imprint","INTERSECT",VERTEX,{"derivedFrom":[subQ1,subQ3]});Q56=makeQuery(id+"F0.imprint","IMPRINT",FACE,{"disambiguationData":[TD([[makeQuery(id+"F0.imprint","IMPRINT",EDGE,{"disambiguationData":[TD([[subQ4,1.0]])],"derivedFrom":subQ3}),-1.0]])]});}
            var Q57;
            {var subQ1=sQuery(id+"F0.wireOp",EDGE,"E9");var subQ3=sQuery(id+"F0.wireOp",EDGE,"iRxx2WUk-GL6D-XYzB-BCGU-y0DAeOXOSD90");var subQ4=makeQuery(id+"F0.imprint","INTERSECT",VERTEX,{"derivedFrom":[subQ1,subQ3]});Q57=makeQuery(id+"F0.imprint","IMPRINT",FACE,{"disambiguationData":[TD([[makeQuery(id+"F0.imprint","IMPRINT",EDGE,{"disambiguationData":[TD([[subQ4,-1.0]])],"derivedFrom":subQ3}),1.0]])]});}
            var Q58;
            {var subQ1=sQuery(id+"F0.wireOp",EDGE,"E9");var subQ3=sQuery(id+"F0.wireOp",EDGE,"iRxx2WUk-GL6D-XYzB-BCGU-y0DAeOXOSD90");var subQ4=makeQuery(id+"F0.imprint","INTERSECT",VERTEX,{"derivedFrom":[subQ1,subQ3]});Q58=makeQuery(id+"F0.imprint","IMPRINT",FACE,{"disambiguationData":[TD([[makeQuery(id+"F0.imprint","IMPRINT",EDGE,{"disambiguationData":[TD([[subQ4,-1.0]])],"derivedFrom":subQ3}),-1.0]])]});}
            var Q59;
            {var subQ1=sQuery(id+"F0.wireOp",EDGE,"E9");var subQ3=sQuery(id+"F0.wireOp",EDGE,"E25");var subQ4=makeQuery(id+"F0.imprint","INTERSECT",VERTEX,{"derivedFrom":[subQ1,subQ3]});Q59=makeQuery(id+"F0.imprint","IMPRINT",FACE,{"disambiguationData":[TD([[makeQuery(id+"F0.imprint","IMPRINT",EDGE,{"disambiguationData":[TD([[subQ4,1.0]])],"derivedFrom":subQ3}),-1.0]])]});}
            var Q60;
            {var subQ1=sQuery(id+"F0.wireOp",EDGE,"E9");var subQ3=sQuery(id+"F0.wireOp",EDGE,"E25");var subQ4=makeQuery(id+"F0.imprint","INTERSECT",VERTEX,{"derivedFrom":[subQ1,subQ3]});Q60=makeQuery(id+"F0.imprint","IMPRINT",FACE,{"disambiguationData":[TD([[makeQuery(id+"F0.imprint","IMPRINT",EDGE,{"disambiguationData":[TD([[subQ4,1.0]])],"derivedFrom":subQ3}),1.0]])]});}
            var Q61;
            {var subQ1=sQuery(id+"F0.wireOp",EDGE,"E10");var subQ3=sQuery(id+"F0.wireOp",EDGE,"E43");var subQ4=makeQuery(id+"F0.imprint","INTERSECT",VERTEX,{"disambiguationData":[OD(0.0)],"derivedFrom":[subQ1,subQ3]});Q61=makeQuery(id+"F0.imprint","IMPRINT",FACE,{"disambiguationData":[TD([[makeQuery(id+"F0.imprint","IMPRINT",EDGE,{"disambiguationData":[TD([[subQ4,-1.0]])],"derivedFrom":subQ3}),-1.0]])]});}
            var Q62;
            {var subQ1=sQuery(id+"F0.wireOp",EDGE,"E10");var subQ3=sQuery(id+"F0.wireOp",EDGE,"E43");var subQ4=makeQuery(id+"F0.imprint","INTERSECT",VERTEX,{"disambiguationData":[OD(0.0)],"derivedFrom":[subQ1,subQ3]});Q62=makeQuery(id+"F0.imprint","IMPRINT",FACE,{"disambiguationData":[TD([[makeQuery(id+"F0.imprint","IMPRINT",EDGE,{"disambiguationData":[TD([[subQ4,-1.0]])],"derivedFrom":subQ3}),1.0]])]});}
            var Q63;
            {var subQ0=sQuery(id+"F0.wireOp",EDGE,"E58");var subQ1=sQuery(id+"F0.wireOp",EDGE,"E43");var subQ2=makeQuery(id+"F0.imprint","INTERSECT",VERTEX,{"derivedFrom":[subQ1,subQ0]});Q63=makeQuery(id+"F0.imprint","IMPRINT",FACE,{"disambiguationData":[TD([[makeQuery(id+"F0.imprint","IMPRINT",EDGE,{"disambiguationData":[TD([[subQ2,-1.0]])],"derivedFrom":subQ1}),-1.0]])]});}
            var Q64;
            {var subQ0=sQuery(id+"F0.wireOp",EDGE,"E58");var subQ1=sQuery(id+"F0.wireOp",EDGE,"E43");var subQ2=makeQuery(id+"F0.imprint","INTERSECT",VERTEX,{"derivedFrom":[subQ1,subQ0]});Q64=makeQuery(id+"F0.imprint","IMPRINT",FACE,{"disambiguationData":[TD([[makeQuery(id+"F0.imprint","IMPRINT",EDGE,{"disambiguationData":[TD([[subQ2,-1.0]])],"derivedFrom":subQ1}),1.0]])]});}
            var Q65;
            {var subQ0=sQuery(id+"F0.wireOp",EDGE,"E8.right");Q65=makeQuery(id+"F0.imprint","IMPRINT",FACE,{"disambiguationData":[TD([[makeQuery(id+"F0.imprint","IMPRINT",EDGE,{"derivedFrom":subQ0}),-1.0]])]});}
            var Q66;
            {var subQ0=sQuery(id+"F0.wireOp",EDGE,"E8.left");Q66=makeQuery(id+"F0.imprint","IMPRINT",FACE,{"disambiguationData":[TD([[makeQuery(id+"F0.imprint","IMPRINT",EDGE,{"derivedFrom":subQ0}),1.0]])]});}
            var Q67;
            {var subQ0=sQuery(id+"F0.wireOp",EDGE,"E8.right");Q67=makeQuery(id+"F0.imprint","IMPRINT",FACE,{"disambiguationData":[TD([[makeQuery(id+"F0.imprint","IMPRINT",EDGE,{"derivedFrom":subQ0}),1.0]])]});}
            var Q68;
            {var subQ0=sQuery(id+"F0.wireOp",EDGE,"E54");Q68=makeQuery(id+"F0.imprint","IMPRINT",FACE,{"disambiguationData":[TD([[makeQuery(id+"F0.imprint","IMPRINT",EDGE,{"derivedFrom":subQ0}),1.0]])]});}
            var Q69;
            {var subQ0=sQuery(id+"F0.wireOp",EDGE,"E55");Q69=makeQuery(id+"F0.imprint","IMPRINT",FACE,{"disambiguationData":[TD([[makeQuery(id+"F0.imprint","IMPRINT",EDGE,{"derivedFrom":subQ0}),1.0]])]});}
            var Q70;
            {var subQ0=sQuery(id+"F0.wireOp",EDGE,"PWp1EvH2-qaDC-40DG-vf9U-hu9o8N1M8XT3");Q70=makeQuery(id+"F0.imprint","IMPRINT",FACE,{"disambiguationData":[TD([[makeQuery(id+"F0.imprint","IMPRINT",EDGE,{"derivedFrom":subQ0}),1.0]])]});}
            var Q71;
            {var subQ0=sQuery(id+"F0.wireOp",EDGE,"reiyEHRU-APE3-DGhp-Yd7A-jMOsKlnvIUoY");Q71=makeQuery(id+"F0.imprint","IMPRINT",FACE,{"disambiguationData":[TD([[makeQuery(id+"F0.imprint","IMPRINT",EDGE,{"derivedFrom":subQ0}),1.0]])]});}
            var Q72;
            {var subQ3=sQuery(id+"F0.wireOp",EDGE,"E30");Q72=makeQuery(id+"F0.imprint","IMPRINT",FACE,{"disambiguationData":[TD([[makeQuery(id+"F0.imprint","IMPRINT",EDGE,{"derivedFrom":subQ3}),-1.0]])]});}
            var Q73;
            {var subQ0=sQuery(id+"F0.wireOp",EDGE,"E31");Q73=makeQuery(id+"F0.imprint","IMPRINT",FACE,{"disambiguationData":[TD([[makeQuery(id+"F0.imprint","IMPRINT",EDGE,{"derivedFrom":subQ0}),1.0]])]});}
            var Q74;
            {var subQ0=sQuery(id+"F0.wireOp",EDGE,"E32");var subQ6=sQuery(id+"F0.wireOp",EDGE,"E62");var subQ7=makeQuery(id+"F0.imprint","INTERSECT",VERTEX,{"derivedFrom":[subQ0,subQ6]});Q74=makeQuery(id+"F0.imprint","IMPRINT",FACE,{"disambiguationData":[TD([[makeQuery(id+"F0.imprint","IMPRINT",EDGE,{"disambiguationData":[TD([[subQ7,1.0]])],"derivedFrom":subQ6}),-1.0]])]});}
            var Q75;
            {var subQ0=sQuery(id+"F0.wireOp",EDGE,"E77");var subQ1=sQuery(id+"F0.wireOp",EDGE,"E25");var subQ2=makeQuery(id+"F0.imprint","INTERSECT",VERTEX,{"disambiguationData":[OD(1.0)],"derivedFrom":[subQ1,subQ0]});Q75=makeQuery(id+"F0.imprint","IMPRINT",FACE,{"disambiguationData":[TD([[makeQuery(id+"F0.imprint","IMPRINT",EDGE,{"disambiguationData":[TD([[subQ2,-1.0]])],"derivedFrom":subQ1}),-1.0]])]});}
            var Q76;
            {var subQ1=sQuery(id+"F0.wireOp",EDGE,"E46");var subQ5=sQuery(id+"F0.wireOp",EDGE,"E5.left");var subQ6=makeQuery(id+"F0.imprint","INTERSECT",VERTEX,{"disambiguationData":[OD(1.0)],"derivedFrom":[subQ5,subQ1]});Q76=makeQuery(id+"F0.imprint","IMPRINT",FACE,{"disambiguationData":[TD([[makeQuery(id+"F0.imprint","IMPRINT",EDGE,{"disambiguationData":[TD([[subQ6,1.0]])],"derivedFrom":subQ5}),1.0]])]});}
            var Q77;
            {var subQ1=sQuery(id+"F0.wireOp",EDGE,"E47");var subQ7=sQuery(id+"F0.wireOp",EDGE,"E5.top");var subQ9=makeQuery(id+"F0.imprint","INTERSECT",VERTEX,{"disambiguationData":[OD(1.0)],"derivedFrom":[subQ7,subQ1]});Q77=makeQuery(id+"F0.imprint","IMPRINT",FACE,{"disambiguationData":[TD([[makeQuery(id+"F0.imprint","IMPRINT",EDGE,{"disambiguationData":[TD([[subQ9,1.0]])],"derivedFrom":subQ7}),1.0]])]});}
            var Q78;
            {var subQ1=sQuery(id+"F0.wireOp",EDGE,"E49");var subQ3=sQuery(id+"F0.wireOp",EDGE,"E5.top");var subQ4=makeQuery(id+"F0.imprint","INTERSECT",VERTEX,{"disambiguationData":[OD(1.0)],"derivedFrom":[subQ3,subQ1]});Q78=makeQuery(id+"F0.imprint","IMPRINT",FACE,{"disambiguationData":[TD([[makeQuery(id+"F0.imprint","IMPRINT",EDGE,{"disambiguationData":[TD([[subQ4,1.0]])],"derivedFrom":subQ3}),1.0]])]});}
            var Q79;
            {var subQ5=sQuery(id+"F0.wireOp",EDGE,"E49");var subQ6=sQuery(id+"F0.wireOp",EDGE,"E5.top");var subQ7=makeQuery(id+"F0.imprint","INTERSECT",VERTEX,{"disambiguationData":[OD(0.0)],"derivedFrom":[subQ6,subQ5]});Q79=makeQuery(id+"F0.imprint","IMPRINT",FACE,{"disambiguationData":[TD([[makeQuery(id+"F0.imprint","IMPRINT",EDGE,{"disambiguationData":[TD([[subQ7,-1.0]])],"derivedFrom":subQ6}),1.0]])]});}
            var Q80;
            {var subQ0=sQuery(id+"F0.wireOp",EDGE,"E47");var subQ1=sQuery(id+"F0.wireOp",EDGE,"E5.top");var subQ2=makeQuery(id+"F0.imprint","INTERSECT",VERTEX,{"disambiguationData":[OD(1.0)],"derivedFrom":[subQ1,subQ0]});Q80=makeQuery(id+"F0.imprint","IMPRINT",FACE,{"disambiguationData":[TD([[makeQuery(id+"F0.imprint","IMPRINT",EDGE,{"disambiguationData":[TD([[subQ2,-1.0]])],"derivedFrom":subQ1}),1.0]])]});}
            var Q81;
            {var subQ0=sQuery(id+"F0.wireOp",EDGE,"xTzPpPS7-AWK9-rnpW-Drzp-4mMhHUCgZzYA");var subQ1=sQuery(id+"F0.wireOp",EDGE,"E5.top");var subQ2=makeQuery(id+"F0.imprint","INTERSECT",VERTEX,{"derivedFrom":[subQ1,subQ0]});Q81=makeQuery(id+"F0.imprint","IMPRINT",FACE,{"disambiguationData":[TD([[makeQuery(id+"F0.imprint","IMPRINT",EDGE,{"disambiguationData":[TD([[subQ2,-1.0]])],"derivedFrom":subQ1}),-1.0]])]});}
            var Q82;
            {var subQ0=sQuery(id+"F0.wireOp",EDGE,"E58");var subQ1=sQuery(id+"F0.wireOp",EDGE,"E5.top");var subQ2=makeQuery(id+"F0.imprint","INTERSECT",VERTEX,{"derivedFrom":[subQ1,subQ0]});Q82=makeQuery(id+"F0.imprint","IMPRINT",FACE,{"disambiguationData":[TD([[makeQuery(id+"F0.imprint","IMPRINT",EDGE,{"disambiguationData":[TD([[subQ2,-1.0]])],"derivedFrom":subQ1}),-1.0]])]});}
            var Q83;
            {var subQ1=sQuery(id+"F0.wireOp",EDGE,"E32");var subQ4=sQuery(id+"F0.wireOp",EDGE,"E77");var subQ9=makeQuery(id+"F0.imprint","INTERSECT",VERTEX,{"disambiguationData":[OD(0.0)],"derivedFrom":[subQ1,subQ4]});Q83=makeQuery(id+"F0.imprint","IMPRINT",FACE,{"disambiguationData":[TD([[makeQuery(id+"F0.imprint","IMPRINT",EDGE,{"disambiguationData":[TD([[subQ9,-1.0]])],"derivedFrom":subQ1}),1.0]])]});}
            var Q84;
            {var subQ0=sQuery(id+"F0.wireOp",EDGE,"cPp6gtkD-EIpK-arVb-j6fT-LqVy2L1S3dPX");var subQ1=sQuery(id+"F0.wireOp",EDGE,"E32");var subQ2=makeQuery(id+"F0.imprint","INTERSECT",VERTEX,{"derivedFrom":[subQ1,subQ0]});Q84=makeQuery(id+"F0.imprint","IMPRINT",FACE,{"disambiguationData":[TD([[makeQuery(id+"F0.imprint","IMPRINT",EDGE,{"disambiguationData":[TD([[subQ2,-1.0]])],"derivedFrom":subQ1}),1.0]])]});}
            var Q85;
            {var subQ3=sQuery(id+"F0.wireOp",EDGE,"PHgcqrMN-hn2K-kQwF-AW5i-nnUKIye7lLSX");var subQ5=sQuery(id+"F0.wireOp",EDGE,"E32");var subQ6=makeQuery(id+"F0.imprint","INTERSECT",VERTEX,{"derivedFrom":[subQ5,subQ3]});Q85=makeQuery(id+"F0.imprint","IMPRINT",FACE,{"disambiguationData":[TD([[makeQuery(id+"F0.imprint","IMPRINT",EDGE,{"disambiguationData":[TD([[subQ6,-1.0]])],"derivedFrom":subQ5}),1.0]])]});}
            var Q86;
            {var subQ0=sQuery(id+"F0.wireOp",EDGE,"E46");var subQ1=sQuery(id+"F0.wireOp",EDGE,"E32");var subQ2=makeQuery(id+"F0.imprint","INTERSECT",VERTEX,{"disambiguationData":[OD(1.0)],"derivedFrom":[subQ1,subQ0]});Q86=makeQuery(id+"F0.imprint","IMPRINT",FACE,{"disambiguationData":[TD([[makeQuery(id+"F0.imprint","IMPRINT",EDGE,{"disambiguationData":[TD([[subQ2,-1.0]])],"derivedFrom":subQ1}),1.0]])]});}
            var Q87;
            {var subQ6=sQuery(id+"F0.wireOp",EDGE,"E46");var subQ10=sQuery(id+"F0.wireOp",EDGE,"E32");var subQ12=makeQuery(id+"F0.imprint","INTERSECT",VERTEX,{"disambiguationData":[OD(0.0)],"derivedFrom":[subQ10,subQ6]});Q87=makeQuery(id+"F0.imprint","IMPRINT",FACE,{"disambiguationData":[TD([[makeQuery(id+"F0.imprint","IMPRINT",EDGE,{"disambiguationData":[TD([[subQ12,-1.0]])],"derivedFrom":subQ10}),1.0]])]});}
            var Q88;
            {var subQ7=sQuery(id+"F0.wireOp",EDGE,"E22");Q88=makeQuery(id+"F0.imprint","IMPRINT",FACE,{"disambiguationData":[TD([[makeQuery(id+"F0.imprint","IMPRINT",EDGE,{"derivedFrom":subQ7}),-1.0]])]});}
            var Q89;
            {var subQ5=sQuery(id+"F0.wireOp",EDGE,"E74");Q89=makeQuery(id+"F0.imprint","IMPRINT",FACE,{"disambiguationData":[TD([[makeQuery(id+"F0.imprint","IMPRINT",EDGE,{"derivedFrom":subQ5}),-1.0]])]});}
            var Q90;
            {var subQ0=sQuery(id+"F0.wireOp",EDGE,"E21");Q90=makeQuery(id+"F0.imprint","IMPRINT",FACE,{"disambiguationData":[TD([[makeQuery(id+"F0.imprint","IMPRINT",EDGE,{"derivedFrom":subQ0}),1.0]])]});}
            var Q91;
            {var subQ0=sQuery(id+"F0.wireOp",EDGE,"E20.left");Q91=makeQuery(id+"F0.imprint","IMPRINT",FACE,{"disambiguationData":[TD([[makeQuery(id+"F0.imprint","IMPRINT",EDGE,{"derivedFrom":subQ0}),-1.0]])]});}
            var Q92;
            {var subQ0=sQuery(id+"F0.wireOp",EDGE,"E12");Q92=makeQuery(id+"F0.imprint","IMPRINT",FACE,{"disambiguationData":[TD([[makeQuery(id+"F0.imprint","IMPRINT",EDGE,{"derivedFrom":subQ0}),-1.0]])]});}
            var Q93;
            {var subQ0=sQuery(id+"F0.wireOp",EDGE,"E31");var subQ5=sQuery(id+"F0.wireOp",EDGE,"E68");var subQ6=makeQuery(id+"F0.imprint","INTERSECT",VERTEX,{"derivedFrom":[subQ0,subQ5]});Q93=makeQuery(id+"F0.imprint","IMPRINT",FACE,{"disambiguationData":[TD([[makeQuery(id+"F0.imprint","IMPRINT",EDGE,{"disambiguationData":[TD([[subQ6,1.0]])],"derivedFrom":subQ5}),1.0]])]});}
            var Q94;
            {var subQ0=sQuery(id+"F0.wireOp",EDGE,"E54");var subQ5=sQuery(id+"F0.wireOp",EDGE,"E31");var subQ6=makeQuery(id+"F0.imprint","INTERSECT",VERTEX,{"derivedFrom":[subQ5,subQ0]});Q94=makeQuery(id+"F0.imprint","IMPRINT",FACE,{"disambiguationData":[TD([[makeQuery(id+"F0.imprint","IMPRINT",EDGE,{"disambiguationData":[TD([[subQ6,-1.0]])],"derivedFrom":subQ5}),-1.0]])]});}
            var Q95;
            {var subQ1=sQuery(id+"F0.wireOp",EDGE,"E19");var subQ3=sQuery(id+"F0.wireOp",EDGE,"E68");var subQ4=makeQuery(id+"F0.imprint","INTERSECT",VERTEX,{"disambiguationData":[OD(1.0)],"derivedFrom":[subQ1,subQ3]});Q95=makeQuery(id+"F0.imprint","IMPRINT",FACE,{"disambiguationData":[TD([[makeQuery(id+"F0.imprint","IMPRINT",EDGE,{"disambiguationData":[TD([[subQ4,-1.0]])],"derivedFrom":subQ3}),1.0]])]});}
            var Q96;
            {var subQ0=sQuery(id+"F0.wireOp",EDGE,"PHgcqrMN-hn2K-kQwF-AW5i-nnUKIye7lLSX");var subQ1=sQuery(id+"F0.wireOp",EDGE,"E33");var subQ2=makeQuery(id+"F0.imprint","INTERSECT",VERTEX,{"derivedFrom":[subQ1,subQ0]});Q96=makeQuery(id+"F0.imprint","IMPRINT",FACE,{"disambiguationData":[TD([[makeQuery(id+"F0.imprint","IMPRINT",EDGE,{"disambiguationData":[TD([[subQ2,-1.0]])],"derivedFrom":subQ1}),-1.0]])]});}
            var Q97;
            {var subQ0=sQuery(id+"F0.wireOp",EDGE,"WS1PBysa-2myF-tvuX-9egV-Ii3JKGoMfvYI");var subQ1=sQuery(id+"F0.wireOp",EDGE,"E9");var subQ2=makeQuery(id+"F0.imprint","INTERSECT",VERTEX,{"disambiguationData":[OD(0.0)],"derivedFrom":[subQ1,subQ0]});Q97=makeQuery(id+"F0.imprint","IMPRINT",FACE,{"disambiguationData":[TD([[makeQuery(id+"F0.imprint","IMPRINT",EDGE,{"disambiguationData":[TD([[subQ2,-1.0]])],"derivedFrom":subQ1}),1.0]])]});}
            var Q98;
            {var subQ0=sQuery(id+"F0.wireOp",EDGE,"E49");var subQ1=sQuery(id+"F0.wireOp",EDGE,"E5.right");var subQ2=makeQuery(id+"F0.imprint","INTERSECT",VERTEX,{"disambiguationData":[OD(0.0)],"derivedFrom":[subQ1,subQ0]});Q98=makeQuery(id+"F0.imprint","IMPRINT",FACE,{"disambiguationData":[TD([[makeQuery(id+"F0.imprint","IMPRINT",EDGE,{"disambiguationData":[TD([[subQ2,-1.0]])],"derivedFrom":subQ1}),1.0]])]});}
            var Q99;
            {var subQ0=sQuery(id+"F0.wireOp",EDGE,"E58");var subQ1=sQuery(id+"F0.wireOp",EDGE,"E5.right");var subQ2=makeQuery(id+"F0.imprint","INTERSECT",VERTEX,{"derivedFrom":[subQ1,subQ0]});Q99=makeQuery(id+"F0.imprint","IMPRINT",FACE,{"disambiguationData":[TD([[makeQuery(id+"F0.imprint","IMPRINT",EDGE,{"disambiguationData":[TD([[subQ2,-1.0]])],"derivedFrom":subQ1}),1.0]])]});}
            var Q100;
            {var subQ0=sQuery(id+"F0.wireOp",EDGE,"E49");var subQ1=sQuery(id+"F0.wireOp",EDGE,"E9");var subQ2=makeQuery(id+"F0.imprint","INTERSECT",VERTEX,{"disambiguationData":[OD(0.0)],"derivedFrom":[subQ1,subQ0]});Q100=makeQuery(id+"F0.imprint","IMPRINT",FACE,{"disambiguationData":[TD([[makeQuery(id+"F0.imprint","IMPRINT",EDGE,{"disambiguationData":[TD([[subQ2,-1.0]])],"derivedFrom":subQ1}),1.0]])]});}
            var Q101;
            {var subQ0=sQuery(id+"F0.wireOp",EDGE,"E10");var subQ1=sQuery(id+"F0.wireOp",EDGE,"E5.right");var subQ2=makeQuery(id+"F0.imprint","INTERSECT",VERTEX,{"disambiguationData":[OD(1.0)],"derivedFrom":[subQ1,subQ0]});Q101=makeQuery(id+"F0.imprint","IMPRINT",FACE,{"disambiguationData":[TD([[makeQuery(id+"F0.imprint","IMPRINT",EDGE,{"disambiguationData":[TD([[subQ2,-1.0]])],"derivedFrom":subQ1}),1.0]])]});}
            var Q102;
            {var subQ0=sQuery(id+"F0.wireOp",EDGE,"E5.top");var subQ1=sQuery(id+"F0.wireOp",EDGE,"E3");var subQ2=makeQuery(id+"F0.imprint","INTERSECT",VERTEX,{"disambiguationData":[OD(0.0)],"derivedFrom":[subQ1,subQ0]});Q102=makeQuery(id+"F0.imprint","IMPRINT",FACE,{"disambiguationData":[TD([[makeQuery(id+"F0.imprint","IMPRINT",EDGE,{"disambiguationData":[TD([[subQ2,1.0]])],"derivedFrom":subQ1}),-1.0]])]});}
            var Q103;
            {var subQ1=sQuery(id+"F0.wireOp",EDGE,"E5.top");var subQ5=sQuery(id+"F0.wireOp",EDGE,"E3");var subQ6=makeQuery(id+"F0.imprint","INTERSECT",VERTEX,{"disambiguationData":[OD(1.0)],"derivedFrom":[subQ5,subQ1]});Q103=makeQuery(id+"F0.imprint","IMPRINT",FACE,{"disambiguationData":[TD([[makeQuery(id+"F0.imprint","IMPRINT",EDGE,{"disambiguationData":[TD([[subQ6,1.0]])],"derivedFrom":subQ5}),-1.0]])]});}
            var Q104;
            {var subQ0=sQuery(id+"F0.wireOp",EDGE,"E19");var subQ1=sQuery(id+"F0.wireOp",EDGE,"E5.top");var subQ2=makeQuery(id+"F0.imprint","INTERSECT",VERTEX,{"derivedFrom":[subQ1,subQ0]});Q104=makeQuery(id+"F0.imprint","IMPRINT",FACE,{"disambiguationData":[TD([[makeQuery(id+"F0.imprint","IMPRINT",EDGE,{"disambiguationData":[TD([[subQ2,1.0]])],"derivedFrom":subQ1}),-1.0]])]});}
            var Q105;
            {var subQ0=sQuery(id+"F0.wireOp",EDGE,"E10");var subQ1=sQuery(id+"F0.wireOp",EDGE,"E5.top");var subQ2=makeQuery(id+"F0.imprint","INTERSECT",VERTEX,{"disambiguationData":[OD(0.0)],"derivedFrom":[subQ1,subQ0]});Q105=makeQuery(id+"F0.imprint","IMPRINT",FACE,{"disambiguationData":[TD([[makeQuery(id+"F0.imprint","IMPRINT",EDGE,{"disambiguationData":[TD([[subQ2,1.0]])],"derivedFrom":subQ1}),-1.0]])]});}
            var Q106;
            {var subQ0=sQuery(id+"F0.wireOp",EDGE,"E5.top");var subQ1=sQuery(id+"F0.wireOp",EDGE,"E3");var subQ2=makeQuery(id+"F0.imprint","INTERSECT",VERTEX,{"disambiguationData":[OD(0.0)],"derivedFrom":[subQ1,subQ0]});Q106=makeQuery(id+"F0.imprint","IMPRINT",FACE,{"disambiguationData":[TD([[makeQuery(id+"F0.imprint","IMPRINT",EDGE,{"disambiguationData":[TD([[subQ2,-1.0]])],"derivedFrom":subQ1}),-1.0]])]});}
            var Q107;
            Q107=makeQuery(id+"F0.imprint","IMPRINT",FACE,{"disambiguationData":[TD([[makeQuery(id+"F0.imprint","IMPRINT",EDGE,{"derivedFrom":sQuery(id+"F0.wireOp",EDGE,"E76")}),-1.0]])]});
            var Q108;
            {var subQ0=sQuery(id+"F0.wireOp",EDGE,"E77");var subQ1=sQuery(id+"F0.wireOp",EDGE,"E24");var subQ2=makeQuery(id+"F0.imprint","INTERSECT",VERTEX,{"disambiguationData":[OD(0.0)],"derivedFrom":[subQ1,subQ0]});Q108=makeQuery(id+"F0.imprint","IMPRINT",FACE,{"disambiguationData":[TD([[makeQuery(id+"F0.imprint","IMPRINT",EDGE,{"disambiguationData":[TD([[subQ2,-1.0]])],"derivedFrom":subQ1}),-1.0]])]});}
            var Q109;
            {var subQ0=sQuery(id+"F0.wireOp",EDGE,"E77");var subQ1=sQuery(id+"F0.wireOp",EDGE,"E28");var subQ2=makeQuery(id+"F0.imprint","INTERSECT",VERTEX,{"disambiguationData":[OD(0.0)],"derivedFrom":[subQ1,subQ0]});Q109=makeQuery(id+"F0.imprint","IMPRINT",FACE,{"disambiguationData":[TD([[makeQuery(id+"F0.imprint","IMPRINT",EDGE,{"disambiguationData":[TD([[subQ2,-1.0]])],"derivedFrom":subQ1}),1.0]])]});}
            var Q110;
            {var subQ1=sQuery(id+"F0.wireOp",EDGE,"E7");var subQ3=sQuery(id+"F0.wireOp",EDGE,"E25");var subQ4=makeQuery(id+"F0.imprint","INTERSECT",VERTEX,{"derivedFrom":[subQ1,subQ3]});Q110=makeQuery(id+"F0.imprint","IMPRINT",FACE,{"disambiguationData":[TD([[makeQuery(id+"F0.imprint","IMPRINT",EDGE,{"disambiguationData":[TD([[subQ4,-1.0]])],"derivedFrom":subQ3}),-1.0]])]});}
            var Q111;
            {var subQ1=sQuery(id+"F0.wireOp",EDGE,"E9");var subQ3=sQuery(id+"F0.wireOp",EDGE,"E25");var subQ4=makeQuery(id+"F0.imprint","INTERSECT",VERTEX,{"derivedFrom":[subQ1,subQ3]});Q111=makeQuery(id+"F0.imprint","IMPRINT",FACE,{"disambiguationData":[TD([[makeQuery(id+"F0.imprint","IMPRINT",EDGE,{"disambiguationData":[TD([[subQ4,1.0]])],"derivedFrom":subQ3}),-1.0]])]});}
            var Q112;
            {var subQ1=sQuery(id+"F0.wireOp",EDGE,"E7");var subQ3=sQuery(id+"F0.wireOp",EDGE,"E25");var subQ4=makeQuery(id+"F0.imprint","INTERSECT",VERTEX,{"derivedFrom":[subQ1,subQ3]});Q112=makeQuery(id+"F0.imprint","IMPRINT",FACE,{"disambiguationData":[TD([[makeQuery(id+"F0.imprint","IMPRINT",EDGE,{"disambiguationData":[TD([[subQ4,-1.0]])],"derivedFrom":subQ3}),1.0]])]});}
            var Q113;
            {var subQ1=sQuery(id+"F0.wireOp",EDGE,"E9");var subQ3=sQuery(id+"F0.wireOp",EDGE,"E25");var subQ4=makeQuery(id+"F0.imprint","INTERSECT",VERTEX,{"derivedFrom":[subQ1,subQ3]});Q113=makeQuery(id+"F0.imprint","IMPRINT",FACE,{"disambiguationData":[TD([[makeQuery(id+"F0.imprint","IMPRINT",EDGE,{"disambiguationData":[TD([[subQ4,1.0]])],"derivedFrom":subQ3}),1.0]])]});}
            var Q114;
            {var subQ0=sQuery(id+"F0.wireOp",EDGE,"CJu0q3cJ-UOam-AZgp-zlKw-gfyc6rk8x2OD");Q114=makeQuery(id+"F0.imprint","IMPRINT",FACE,{"disambiguationData":[TD([[makeQuery(id+"F0.imprint","IMPRINT",EDGE,{"derivedFrom":subQ0}),1.0]])]});}
            var Q115;
            {var subQ4=sQuery(id+"F0.wireOp",EDGE,"yiJSfqnx-Zk91-TDUn-W7H7-58YXdiS9JH1e");var subQ6=sQuery(id+"F0.wireOp",EDGE,"E38");var subQ8=makeQuery(id+"F0.imprint","INTERSECT",VERTEX,{"derivedFrom":[subQ6,subQ4]});Q115=makeQuery(id+"F0.imprint","IMPRINT",FACE,{"disambiguationData":[TD([[makeQuery(id+"F0.imprint","IMPRINT",EDGE,{"disambiguationData":[TD([[subQ8,-1.0]])],"derivedFrom":subQ6}),1.0]])]});}
            var Q116;
            {var subQ0=sQuery(id+"F0.wireOp",EDGE,"cDreJq0e-z7uL-DqTs-FtDv-EibUY7lb0aSl");Q116=makeQuery(id+"F0.imprint","IMPRINT",FACE,{"disambiguationData":[TD([[makeQuery(id+"F0.imprint","IMPRINT",EDGE,{"derivedFrom":subQ0}),1.0]])]});}
            var Q117;
            {var subQ3=sQuery(id+"F0.wireOp",EDGE,"E62");var subQ5=sQuery(id+"F0.wireOp",EDGE,"E40");var subQ6=makeQuery(id+"F0.imprint","INTERSECT",VERTEX,{"derivedFrom":[subQ5,subQ3]});Q117=makeQuery(id+"F0.imprint","IMPRINT",FACE,{"disambiguationData":[TD([[makeQuery(id+"F0.imprint","IMPRINT",EDGE,{"disambiguationData":[TD([[subQ6,-1.0]])],"derivedFrom":subQ5}),-1.0]])]});}
            var Q118;
            {var subQ0=sQuery(id+"F0.wireOp",EDGE,"8Gq5NJWu-BzSJ-eRZc-OMQX-WEsSRfLAUc8L");Q118=makeQuery(id+"F0.imprint","IMPRINT",FACE,{"disambiguationData":[TD([[makeQuery(id+"F0.imprint","IMPRINT",EDGE,{"derivedFrom":subQ0}),-1.0]])]});}
            var Q119;
            {var subQ4=sQuery(id+"F0.wireOp",EDGE,"PVwGM4L0-uV6x-An82-xA5I-MeRCTjVu4x1Z");var subQ6=sQuery(id+"F0.wireOp",EDGE,"E40");var subQ7=makeQuery(id+"F0.imprint","INTERSECT",VERTEX,{"derivedFrom":[subQ6,subQ4]});Q119=makeQuery(id+"F0.imprint","IMPRINT",FACE,{"disambiguationData":[TD([[makeQuery(id+"F0.imprint","IMPRINT",EDGE,{"disambiguationData":[TD([[subQ7,-1.0]])],"derivedFrom":subQ6}),-1.0]])]});}
            var Q120;
            {var subQ0=sQuery(id+"F0.wireOp",EDGE,"Zivym9IV-UAFz-mZ4u-rzHU-Z1ZnytKNI18B");var subQ1=sQuery(id+"F0.wireOp",EDGE,"E5.left");var subQ2=makeQuery(id+"F0.imprint","INTERSECT",VERTEX,{"derivedFrom":[subQ1,subQ0]});Q120=makeQuery(id+"F0.imprint","IMPRINT",FACE,{"disambiguationData":[TD([[makeQuery(id+"F0.imprint","IMPRINT",EDGE,{"disambiguationData":[TD([[subQ2,-1.0]])],"derivedFrom":subQ1}),1.0]])]});}
            var Q121;
            {var subQ0=sQuery(id+"F0.wireOp",EDGE,"Zivym9IV-UAFz-mZ4u-rzHU-Z1ZnytKNI18B");var subQ1=sQuery(id+"F0.wireOp",EDGE,"E5.left");var subQ2=makeQuery(id+"F0.imprint","INTERSECT",VERTEX,{"derivedFrom":[subQ1,subQ0]});Q121=makeQuery(id+"F0.imprint","IMPRINT",FACE,{"disambiguationData":[TD([[makeQuery(id+"F0.imprint","IMPRINT",EDGE,{"disambiguationData":[TD([[subQ2,-1.0]])],"derivedFrom":subQ1}),-1.0]])]});}
            var Q122;
            {var subQ0=sQuery(id+"F0.wireOp",EDGE,"rizNNfOU-ZcdL-ylTW-MaPL-rRgeXOHZfHI3");Q122=makeQuery(id+"F0.imprint","IMPRINT",FACE,{"disambiguationData":[TD([[makeQuery(id+"F0.imprint","IMPRINT",EDGE,{"derivedFrom":subQ0}),-1.0]])]});}
            var Q123;
            {var subQ0=sQuery(id+"F0.wireOp",EDGE,"xTzPpPS7-AWK9-rnpW-Drzp-4mMhHUCgZzYA");Q123=makeQuery(id+"F0.imprint","IMPRINT",FACE,{"disambiguationData":[TD([[makeQuery(id+"F0.imprint","IMPRINT",EDGE,{"derivedFrom":subQ0}),1.0]])]});}
            var Q124;
            {var subQ0=sQuery(id+"F0.wireOp",EDGE,"E80");var subQ1=sQuery(id+"F0.wireOp",EDGE,"E5.top");var subQ2=makeQuery(id+"F0.imprint","INTERSECT",VERTEX,{"derivedFrom":[subQ1,subQ0]});Q124=makeQuery(id+"F0.imprint","IMPRINT",FACE,{"disambiguationData":[TD([[makeQuery(id+"F0.imprint","IMPRINT",EDGE,{"disambiguationData":[TD([[subQ2,1.0]])],"derivedFrom":subQ1}),1.0]])]});}
            var Q125;
            {var subQ0=sQuery(id+"F0.wireOp",EDGE,"E60");var subQ1=sQuery(id+"F0.wireOp",EDGE,"E5.top");var subQ2=makeQuery(id+"F0.imprint","INTERSECT",VERTEX,{"derivedFrom":[subQ1,subQ0]});Q125=makeQuery(id+"F0.imprint","IMPRINT",FACE,{"disambiguationData":[TD([[makeQuery(id+"F0.imprint","IMPRINT",EDGE,{"disambiguationData":[TD([[subQ2,-1.0]])],"derivedFrom":subQ1}),-1.0]])]});}
            var Q126;
            {var subQ0=sQuery(id+"F0.wireOp",EDGE,"E36");var subQ1=sQuery(id+"F0.wireOp",EDGE,"E5.left");var subQ2=makeQuery(id+"F0.imprint","INTERSECT",VERTEX,{"disambiguationData":[OD(1.0)],"derivedFrom":[subQ1,subQ0]});Q126=makeQuery(id+"F0.imprint","IMPRINT",FACE,{"disambiguationData":[TD([[makeQuery(id+"F0.imprint","IMPRINT",EDGE,{"disambiguationData":[TD([[subQ2,-1.0]])],"derivedFrom":subQ1}),1.0]])]});}
            var Q127;
            {var subQ0=sQuery(id+"F0.wireOp",EDGE,"E87");Q127=makeQuery(id+"F0.imprint","IMPRINT",FACE,{"disambiguationData":[TD([[makeQuery(id+"F0.imprint","IMPRINT",EDGE,{"derivedFrom":subQ0}),-1.0]])]});}
            var Q128;
            {var subQ0=sQuery(id+"F0.wireOp",EDGE,"E67");var subQ1=sQuery(id+"F0.wireOp",EDGE,"E7");var subQ2=makeQuery(id+"F0.imprint","INTERSECT",VERTEX,{"disambiguationData":[OD(0.0)],"derivedFrom":[subQ1,subQ0]});Q128=makeQuery(id+"F0.imprint","IMPRINT",FACE,{"disambiguationData":[TD([[makeQuery(id+"F0.imprint","IMPRINT",EDGE,{"disambiguationData":[TD([[subQ2,-1.0]])],"derivedFrom":subQ1}),-1.0]])]});}
            var Q129;
            Q129=makeQuery(id+"F0.imprint","IMPRINT",FACE,{"disambiguationData":[TD([[makeQuery(id+"F0.imprint","IMPRINT",EDGE,{"derivedFrom":sQuery(id+"F0.wireOp",EDGE,"E45")}),-1.0]])]});
            var Q130;
            Q130=makeQuery(id+"F0.imprint","IMPRINT",FACE,{"disambiguationData":[TD([[makeQuery(id+"F0.imprint","IMPRINT",EDGE,{"derivedFrom":sQuery(id+"F0.wireOp",EDGE,"E34")}),-1.0]])]});
            var Q131;
            {var subQ4=sQuery(id+"F0.wireOp",EDGE,"E11");Q131=makeQuery(id+"F0.imprint","IMPRINT",FACE,{"disambiguationData":[TD([[makeQuery(id+"F0.imprint","IMPRINT",EDGE,{"derivedFrom":subQ4}),-1.0]])]});}
            var Q132;
            {var subQ5=sQuery(id+"F0.wireOp",EDGE,"E81");Q132=makeQuery(id+"F0.imprint","IMPRINT",FACE,{"disambiguationData":[TD([[makeQuery(id+"F0.imprint","IMPRINT",EDGE,{"derivedFrom":subQ5}),1.0]])]});}
            var Q133;
            {var subQ0=sQuery(id+"F0.wireOp",EDGE,"E10");var subQ1=sQuery(id+"F0.wireOp",EDGE,"E5.top");var subQ2=makeQuery(id+"F0.imprint","INTERSECT",VERTEX,{"disambiguationData":[OD(0.0)],"derivedFrom":[subQ1,subQ0]});Q133=makeQuery(id+"F0.imprint","IMPRINT",FACE,{"disambiguationData":[TD([[makeQuery(id+"F0.imprint","IMPRINT",EDGE,{"disambiguationData":[TD([[subQ2,-1.0]])],"derivedFrom":subQ1}),-1.0]])]});}
            var Q134;
            {var subQ7=sQuery(id+"F0.wireOp",EDGE,"E43");var subQ8=sQuery(id+"F0.wireOp",EDGE,"E4");var subQ9=makeQuery(id+"F0.imprint","INTERSECT",VERTEX,{"disambiguationData":[OD(0.0)],"derivedFrom":[subQ8,subQ7]});Q134=makeQuery(id+"F0.imprint","IMPRINT",FACE,{"disambiguationData":[TD([[makeQuery(id+"F0.imprint","IMPRINT",EDGE,{"disambiguationData":[TD([[subQ9,-1.0]])],"derivedFrom":subQ8}),-1.0]])]});}
            var Q135;
            {var subQ0=sQuery(id+"F0.wireOp",EDGE,"E79");Q135=makeQuery(id+"F0.imprint","IMPRINT",FACE,{"disambiguationData":[TD([[makeQuery(id+"F0.imprint","IMPRINT",EDGE,{"derivedFrom":subQ0}),-1.0]])]});}
            var Q136;
            Q136=makeQuery(id+"F0.imprint","IMPRINT",FACE,{"disambiguationData":[TD([[makeQuery(id+"F0.imprint","IMPRINT",EDGE,{"derivedFrom":sQuery(id+"F0.wireOp",EDGE,"E41")}),-1.0]])]});
            var Q137;
            {var subQ0=sQuery(id+"F0.wireOp",EDGE,"E78");Q137=makeQuery(id+"F0.imprint","IMPRINT",FACE,{"disambiguationData":[TD([[makeQuery(id+"F0.imprint","IMPRINT",EDGE,{"derivedFrom":subQ0}),-1.0]])]});}
            var Q138;
            Q138=makeQuery(id+"F0.imprint","IMPRINT",FACE,{"disambiguationData":[TD([[makeQuery(id+"F0.imprint","IMPRINT",EDGE,{"derivedFrom":sQuery(id+"F0.wireOp",EDGE,"E42")}),-1.0]])]});
            var Q139;
            {var subQ0=sQuery(id+"F0.wireOp",EDGE,"E17");Q139=makeQuery(id+"F0.imprint","IMPRINT",FACE,{"disambiguationData":[TD([[makeQuery(id+"F0.imprint","IMPRINT",EDGE,{"derivedFrom":subQ0}),1.0]])]});}
            var Q140;
            {var subQ0=sQuery(id+"F0.wireOp",EDGE,"E52");Q140=makeQuery(id+"F0.imprint","IMPRINT",FACE,{"disambiguationData":[TD([[makeQuery(id+"F0.imprint","IMPRINT",EDGE,{"derivedFrom":subQ0}),1.0]])]});}
            var Q141;
            {var subQ0=sQuery(id+"F0.wireOp",EDGE,"E39");Q141=makeQuery(id+"F0.imprint","IMPRINT",FACE,{"disambiguationData":[TD([[makeQuery(id+"F0.imprint","IMPRINT",EDGE,{"derivedFrom":subQ0}),1.0]])]});}
            var Q142;
            {var subQ8=sQuery(id+"F0.wireOp",EDGE,"E29");Q142=makeQuery(id+"F0.imprint","IMPRINT",FACE,{"disambiguationData":[TD([[makeQuery(id+"F0.imprint","IMPRINT",EDGE,{"derivedFrom":subQ8}),-1.0]])]});}
            var Q143;
            {var subQ5=sQuery(id+"F0.wireOp",EDGE,"E23");Q143=makeQuery(id+"F0.imprint","IMPRINT",FACE,{"disambiguationData":[TD([[makeQuery(id+"F0.imprint","IMPRINT",EDGE,{"derivedFrom":subQ5}),-1.0]])]});}
            var Q144;
            {var subQ0=sQuery(id+"F0.wireOp",EDGE,"E67");var subQ1=sQuery(id+"F0.wireOp",EDGE,"E7");var subQ2=makeQuery(id+"F0.imprint","INTERSECT",VERTEX,{"disambiguationData":[OD(0.0)],"derivedFrom":[subQ1,subQ0]});Q144=makeQuery(id+"F0.imprint","IMPRINT",FACE,{"disambiguationData":[TD([[makeQuery(id+"F0.imprint","IMPRINT",EDGE,{"disambiguationData":[TD([[subQ2,-1.0]])],"derivedFrom":subQ1}),1.0]])]});}
            var Q145;
            {var subQ0=sQuery(id+"F0.wireOp",EDGE,"E8.left");Q145=makeQuery(id+"F0.imprint","IMPRINT",FACE,{"disambiguationData":[TD([[makeQuery(id+"F0.imprint","IMPRINT",EDGE,{"derivedFrom":subQ0}),-1.0]])]});}
            var Q146;
            {var subQ0=sQuery(id+"F0.wireOp",EDGE,"E94");Q146=makeQuery(id+"F0.imprint","IMPRINT",FACE,{"disambiguationData":[TD([[makeQuery(id+"F0.imprint","IMPRINT",EDGE,{"derivedFrom":subQ0}),-1.0]])]});}
            var Q147;
            {var subQ7=sQuery(id+"F0.wireOp",EDGE,"E96");Q147=makeQuery(id+"F0.imprint","IMPRINT",FACE,{"disambiguationData":[TD([[makeQuery(id+"F0.imprint","IMPRINT",EDGE,{"derivedFrom":subQ7}),-1.0]])]});}
            var Q148;
            {var subQ0=sQuery(id+"F0.wireOp",EDGE,"E92");var subQ1=sQuery(id+"F0.wireOp",EDGE,"E7");var subQ2=makeQuery(id+"F0.imprint","INTERSECT",VERTEX,{"derivedFrom":[subQ1,subQ0]});Q148=makeQuery(id+"F0.imprint","IMPRINT",FACE,{"disambiguationData":[TD([[makeQuery(id+"F0.imprint","IMPRINT",EDGE,{"disambiguationData":[TD([[subQ2,-1.0]])],"derivedFrom":subQ1}),-1.0]])]});}
            var Q149;
            {var subQ5=sQuery(id+"F0.wireOp",EDGE,"E73");Q149=makeQuery(id+"F0.imprint","IMPRINT",FACE,{"disambiguationData":[TD([[makeQuery(id+"F0.imprint","IMPRINT",EDGE,{"derivedFrom":subQ5}),1.0]])]});}
            var Q150;
            {var subQ0=sQuery(id+"F0.wireOp",EDGE,"E66");var subQ1=sQuery(id+"F0.wireOp",EDGE,"E6");var subQ2=makeQuery(id+"F0.imprint","INTERSECT",VERTEX,{"disambiguationData":[OD(0.0)],"derivedFrom":[subQ1,subQ0]});Q150=makeQuery(id+"F0.imprint","IMPRINT",FACE,{"disambiguationData":[TD([[makeQuery(id+"F0.imprint","IMPRINT",EDGE,{"disambiguationData":[TD([[subQ2,-1.0]])],"derivedFrom":subQ1}),1.0]])]});}
            var Q151;
            {var subQ0=sQuery(id+"F0.wireOp",EDGE,"E63");var subQ1=sQuery(id+"F0.wireOp",EDGE,"E7");var subQ2=makeQuery(id+"F0.imprint","INTERSECT",VERTEX,{"disambiguationData":[OD(0.0)],"derivedFrom":[subQ1,subQ0]});Q151=makeQuery(id+"F0.imprint","IMPRINT",FACE,{"disambiguationData":[TD([[makeQuery(id+"F0.imprint","IMPRINT",EDGE,{"disambiguationData":[TD([[subQ2,-1.0]])],"derivedFrom":subQ1}),1.0]])]});}
            var Q152;
            {var subQ0=sQuery(id+"F0.wireOp",EDGE,"E63");var subQ1=sQuery(id+"F0.wireOp",EDGE,"E7");var subQ2=makeQuery(id+"F0.imprint","INTERSECT",VERTEX,{"disambiguationData":[OD(0.0)],"derivedFrom":[subQ1,subQ0]});Q152=makeQuery(id+"F0.imprint","IMPRINT",FACE,{"disambiguationData":[TD([[makeQuery(id+"F0.imprint","IMPRINT",EDGE,{"disambiguationData":[TD([[subQ2,1.0]])],"derivedFrom":subQ1}),1.0]])]});}
            var Q153;
            Q153=makeQuery(id+"F0.imprint","IMPRINT",FACE,{"disambiguationData":[TD([[makeQuery(id+"F0.imprint","IMPRINT",EDGE,{"derivedFrom":sQuery(id+"F0.wireOp",EDGE,"E35")}),-1.0]])]});
            var Q154;
            {var subQ7=sQuery(id+"F0.wireOp",EDGE,"E72");Q154=makeQuery(id+"F0.imprint","IMPRINT",FACE,{"disambiguationData":[TD([[makeQuery(id+"F0.imprint","IMPRINT",EDGE,{"derivedFrom":subQ7}),1.0]])]});}
            var Q155;
            {var subQ0=sQuery(id+"F0.wireOp",EDGE,"E89");Q155=makeQuery(id+"F0.imprint","IMPRINT",FACE,{"disambiguationData":[TD([[makeQuery(id+"F0.imprint","IMPRINT",EDGE,{"derivedFrom":subQ0}),1.0]])]});}
            var Q156;
            {var subQ6=sQuery(id+"F0.wireOp",EDGE,"E5.top");var subQ7=sQuery(id+"F0.wireOp",EDGE,"E2");var subQ12=makeQuery(id+"F0.imprint","INTERSECT",VERTEX,{"disambiguationData":[OD(0.0)],"derivedFrom":[subQ7,subQ6]});Q156=makeQuery(id+"F0.imprint","IMPRINT",FACE,{"disambiguationData":[TD([[makeQuery(id+"F0.imprint","IMPRINT",EDGE,{"disambiguationData":[TD([[subQ12,1.0]])],"derivedFrom":subQ7}),-1.0]])]});}
            var Q157;
            {var subQ0=sQuery(id+"F0.wireOp",EDGE,"E69");Q157=makeQuery(id+"F0.imprint","IMPRINT",FACE,{"disambiguationData":[TD([[makeQuery(id+"F0.imprint","IMPRINT",EDGE,{"derivedFrom":subQ0}),-1.0]])]});}
            var Q158;
            {var subQ0=sQuery(id+"F0.wireOp",EDGE,"E85");Q158=makeQuery(id+"F0.imprint","IMPRINT",FACE,{"disambiguationData":[TD([[makeQuery(id+"F0.imprint","IMPRINT",EDGE,{"derivedFrom":subQ0}),-1.0]])]});}
            var Q159;
            {var subQ0=sQuery(id+"F0.wireOp",EDGE,"E83");Q159=makeQuery(id+"F0.imprint","IMPRINT",FACE,{"disambiguationData":[TD([[makeQuery(id+"F0.imprint","IMPRINT",EDGE,{"derivedFrom":subQ0}),-1.0]])]});}
            var Q160;
            {var subQ4=sQuery(id+"F0.wireOp",EDGE,"T15sGdJh-UEot-Dk7n-Sm4Y-LHUBvKX4WVDX");var subQ5=sQuery(id+"F0.wireOp",EDGE,"E1");var subQ11=makeQuery(id+"F0.imprint","INTERSECT",VERTEX,{"disambiguationData":[OD(0.0)],"derivedFrom":[subQ5,subQ4]});Q160=makeQuery(id+"F0.imprint","IMPRINT",FACE,{"disambiguationData":[TD([[makeQuery(id+"F0.imprint","IMPRINT",EDGE,{"disambiguationData":[TD([[subQ11,-1.0]])],"derivedFrom":subQ5}),-1.0]])]});}
            var Q161;
            {var subQ1=sQuery(id+"F0.wireOp",EDGE,"E6");var subQ9=sQuery(id+"F0.wireOp",EDGE,"Vuoyf5yW-RdsD-7KwS-aWuJ-A4pQkfCWVKX2");var subQ10=makeQuery(id+"F0.imprint","INTERSECT",VERTEX,{"disambiguationData":[OD(1.0)],"derivedFrom":[subQ1,subQ9]});Q161=makeQuery(id+"F0.imprint","IMPRINT",FACE,{"disambiguationData":[TD([[makeQuery(id+"F0.imprint","IMPRINT",EDGE,{"disambiguationData":[TD([[subQ10,-1.0]])],"derivedFrom":subQ1}),-1.0]])]});}
            var Q162;
            {var subQ0=sQuery(id+"F0.wireOp",EDGE,"T15sGdJh-UEot-Dk7n-Sm4Y-LHUBvKX4WVDX");var subQ1=sQuery(id+"F0.wireOp",EDGE,"E7");var subQ2=makeQuery(id+"F0.imprint","INTERSECT",VERTEX,{"disambiguationData":[OD(0.0)],"derivedFrom":[subQ1,subQ0]});Q162=makeQuery(id+"F0.imprint","IMPRINT",FACE,{"disambiguationData":[TD([[makeQuery(id+"F0.imprint","IMPRINT",EDGE,{"disambiguationData":[TD([[subQ2,-1.0]])],"derivedFrom":subQ1}),1.0]])]});}
            var Q163;
            {var subQ0=sQuery(id+"F0.wireOp",EDGE,"E7");var subQ1=makeQuery(id+"F0.imprint","INTERSECT",VERTEX,{"derivedFrom":[subQ0,sQuery(id+"F0.wireOp",EDGE,"E72")]});Q163=makeQuery(id+"F0.imprint","IMPRINT",FACE,{"disambiguationData":[TD([[makeQuery(id+"F0.imprint","IMPRINT",EDGE,{"disambiguationData":[TD([[subQ1,-1.0]])],"derivedFrom":subQ0}),1.0]])]});}
            var Q164;
            {var subQ0=sQuery(id+"F0.wireOp",EDGE,"1kOJtIEV-tiSi-Ut0R-aIPO-QJhH86I71jHU");var subQ1=sQuery(id+"F0.wireOp",EDGE,"E40");var subQ2=makeQuery(id+"F0.imprint","INTERSECT",VERTEX,{"disambiguationData":[OD(0.0)],"derivedFrom":[subQ1,subQ0]});Q164=makeQuery(id+"F0.imprint","IMPRINT",FACE,{"disambiguationData":[TD([[makeQuery(id+"F0.imprint","IMPRINT",EDGE,{"disambiguationData":[TD([[subQ2,-1.0]])],"derivedFrom":subQ1}),1.0]])]});}
            var Q165;
            {var subQ1=sQuery(id+"F0.wireOp",EDGE,"E6");var subQ3=sQuery(id+"F0.wireOp",EDGE,"T15sGdJh-UEot-Dk7n-Sm4Y-LHUBvKX4WVDX");var subQ4=makeQuery(id+"F0.imprint","INTERSECT",VERTEX,{"disambiguationData":[OD(0.0)],"derivedFrom":[subQ1,subQ3]});Q165=makeQuery(id+"F0.imprint","IMPRINT",FACE,{"disambiguationData":[TD([[makeQuery(id+"F0.imprint","IMPRINT",EDGE,{"disambiguationData":[TD([[subQ4,-1.0]])],"derivedFrom":subQ3}),1.0]])]});}
            var Q166;
            {var subQ0=sQuery(id+"F0.wireOp",EDGE,"E37");var subQ1=sQuery(id+"F0.wireOp",EDGE,"E6");var subQ2=makeQuery(id+"F0.imprint","INTERSECT",VERTEX,{"disambiguationData":[OD(0.0)],"derivedFrom":[subQ1,subQ0]});Q166=makeQuery(id+"F0.imprint","IMPRINT",FACE,{"disambiguationData":[TD([[makeQuery(id+"F0.imprint","IMPRINT",EDGE,{"disambiguationData":[TD([[subQ2,-1.0]])],"derivedFrom":subQ1}),1.0]])]});}
            extrude(context, id + "F1", {"entities" : qUnion([Q0, Q1, Q2, Q3, Q4, Q5, Q6, Q7, Q8, Q9, Q10, Q11, Q12, Q13, Q14, Q15, Q16, Q17, Q18, Q19, Q20, Q21, Q22, Q23, Q24, Q25, Q26, Q27, Q28, Q29, Q30, Q31, Q32, Q33, Q34, Q35, Q36, Q37, Q38, Q39, Q40, Q41, Q42, Q43, Q44, Q45, Q46, Q47, Q48, Q49, Q50, Q51, Q52, Q53, Q54, Q55, Q56, Q57, Q58, Q59, Q60, Q61, Q62, Q63, Q64, Q65, Q66, Q67, Q68, Q69, Q70, Q71, Q72, Q73, Q74, Q75, Q76, Q77, Q78, Q79, Q80, Q81, Q82, Q83, Q84, Q85, Q86, Q87, Q88, Q89, Q90, Q91, Q92, Q93, Q94, Q95, Q96, Q97, Q98, Q99, Q100, Q101, Q102, Q103, Q104, Q105, Q106, Q107, Q108, Q109, Q110, Q111, Q112, Q113, Q114, Q115, Q116, Q117, Q118, Q119, Q120, Q121, Q122, Q123, Q124, Q125, Q126, Q127, Q128, Q129, Q130, Q131, Q132, Q133, Q134, Q135, Q136, Q137, Q138, Q139, Q140, Q141, Q142, Q143, Q144, Q145, Q146, Q147, Q148, Q149, Q150, Q151, Q152, Q153, Q154, Q155, Q156, Q157, Q158, Q159, Q160, Q161, Q162, Q163, Q164, Q165, Q166]), "depth" : 6.35 * mm, "offsetDistance" : 25.4 * mm});
        }
    });
